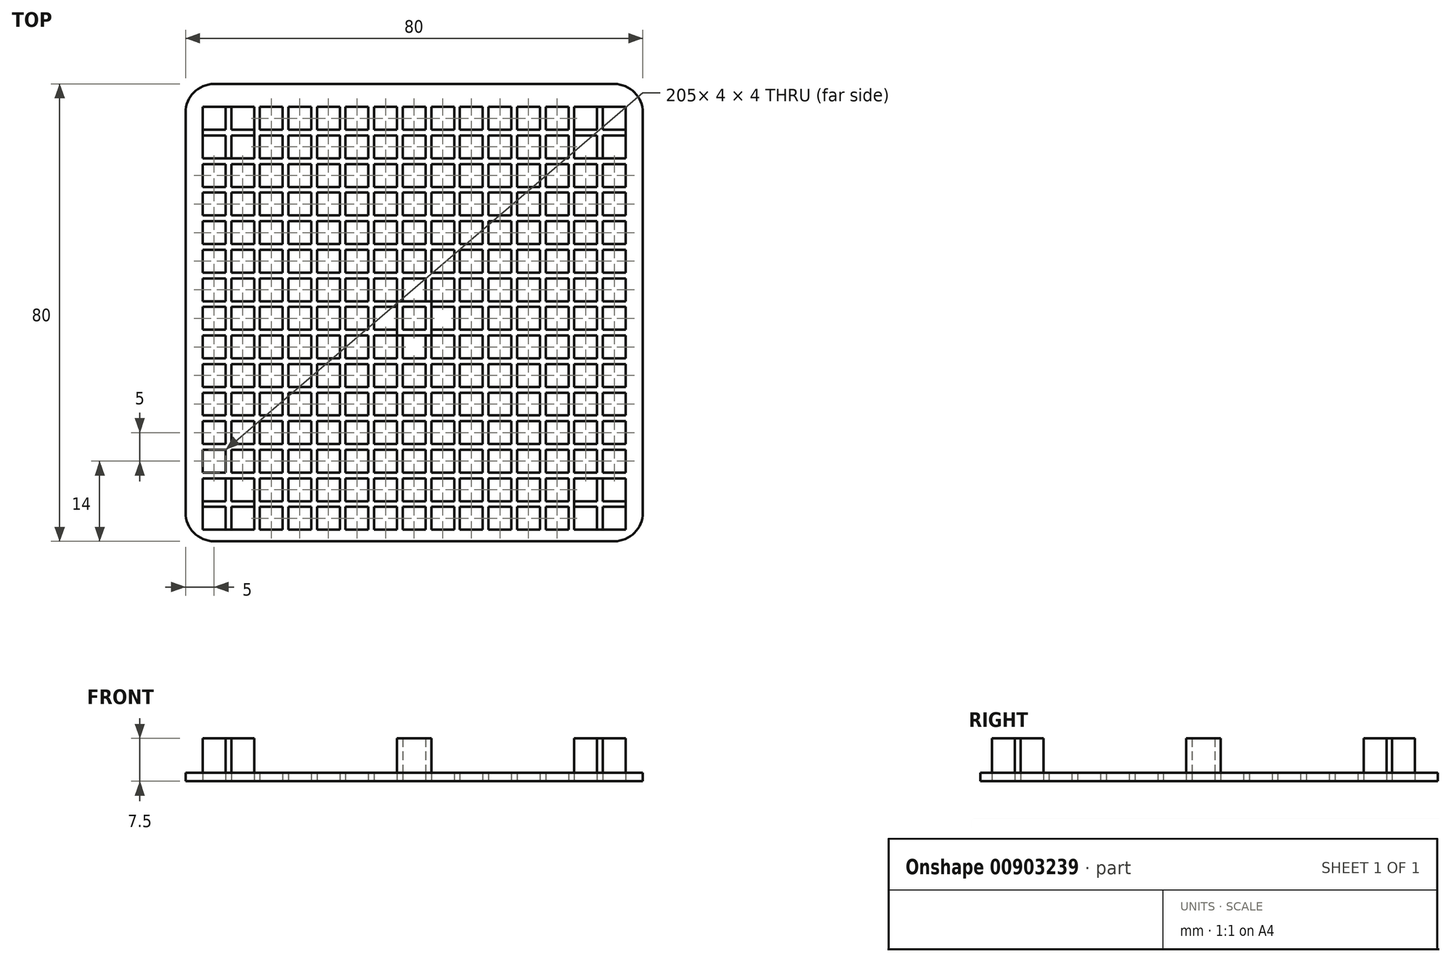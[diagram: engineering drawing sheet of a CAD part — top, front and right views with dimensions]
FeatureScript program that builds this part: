
annotation { "Feature Type Name" : "Feature", "Feature Type Description" : "" }
export const myFeature = defineFeature(function(context is Context, id is Id, definition is map)
    precondition{}
    {
        {
            var Q0;
            Q0=qCreatedBy(makeId("Top.planeOp"),FACE);
            var sketch = newSketch(context, id + "F0", { "sketchPlane" : qUnion([Q0])});
            skLineSegment(sketch, "E0.bottom", {"start": v(40, 40) * mm, "end": v(-40, 40) * mm});
            skLineSegment(sketch, "E0.top", {"start": v(40, -40) * mm, "end": v(-40, -40) * mm});
            skLineSegment(sketch, "E0.left", {"start": v(40, 40) * mm, "end": v(40, -40) * mm});
            skLineSegment(sketch, "E0.right", {"start": v(-40, 40) * mm, "end": v(-40, -40) * mm});
            skPoint(sketch, "E0.middle", {"position": v(0, 0) * mm});
            skLineSegment(sketch, "E1.bottom", {"start": v(-37, 36) * mm, "end": v(-33, 36) * mm});
            skLineSegment(sketch, "E1.top", {"start": v(-37, 32) * mm, "end": v(-33, 32) * mm});
            skLineSegment(sketch, "E1.left", {"start": v(-37, 36) * mm, "end": v(-37, 32) * mm});
            skLineSegment(sketch, "E1.right", {"start": v(-33, 36) * mm, "end": v(-33, 32) * mm});
            skLineSegment(sketch, "E2.0.1.0", {"start": v(-33, 31) * mm, "end": v(-33, 27) * mm});
            skLineSegment(sketch, "E2.0.1.1", {"start": v(-37, 31) * mm, "end": v(-33, 31) * mm});
            skLineSegment(sketch, "E2.0.1.2", {"start": v(-37, 27) * mm, "end": v(-33, 27) * mm});
            skLineSegment(sketch, "E2.0.1.3", {"start": v(-37, 31) * mm, "end": v(-37, 27) * mm});
            skLineSegment(sketch, "E2.0.2.0", {"start": v(-33, 26) * mm, "end": v(-33, 22) * mm});
            skLineSegment(sketch, "E2.0.2.1", {"start": v(-37, 26) * mm, "end": v(-33, 26) * mm});
            skLineSegment(sketch, "E2.0.2.2", {"start": v(-37, 22) * mm, "end": v(-33, 22) * mm});
            skLineSegment(sketch, "E2.0.2.3", {"start": v(-37, 26) * mm, "end": v(-37, 22) * mm});
            skLineSegment(sketch, "E2.0.3.0", {"start": v(-33, 21) * mm, "end": v(-33, 17) * mm});
            skLineSegment(sketch, "E2.0.3.1", {"start": v(-37, 21) * mm, "end": v(-33, 21) * mm});
            skLineSegment(sketch, "E2.0.3.2", {"start": v(-37, 17) * mm, "end": v(-33, 17) * mm});
            skLineSegment(sketch, "E2.0.3.3", {"start": v(-37, 21) * mm, "end": v(-37, 17) * mm});
            skLineSegment(sketch, "E2.0.4.0", {"start": v(-33, 16) * mm, "end": v(-33, 12) * mm});
            skLineSegment(sketch, "E2.0.4.1", {"start": v(-37, 16) * mm, "end": v(-33, 16) * mm});
            skLineSegment(sketch, "E2.0.4.2", {"start": v(-37, 12) * mm, "end": v(-33, 12) * mm});
            skLineSegment(sketch, "E2.0.4.3", {"start": v(-37, 16) * mm, "end": v(-37, 12) * mm});
            skLineSegment(sketch, "E2.0.5.0", {"start": v(-33, 11) * mm, "end": v(-33, 7) * mm});
            skLineSegment(sketch, "E2.0.5.1", {"start": v(-37, 11) * mm, "end": v(-33, 11) * mm});
            skLineSegment(sketch, "E2.0.5.2", {"start": v(-37, 7) * mm, "end": v(-33, 7) * mm});
            skLineSegment(sketch, "E2.0.5.3", {"start": v(-37, 11) * mm, "end": v(-37, 7) * mm});
            skLineSegment(sketch, "E2.0.6.0", {"start": v(-33, 6) * mm, "end": v(-33, 2) * mm});
            skLineSegment(sketch, "E2.0.6.1", {"start": v(-37, 6) * mm, "end": v(-33, 6) * mm});
            skLineSegment(sketch, "E2.0.6.2", {"start": v(-37, 2) * mm, "end": v(-33, 2) * mm});
            skLineSegment(sketch, "E2.0.6.3", {"start": v(-37, 6) * mm, "end": v(-37, 2) * mm});
            skLineSegment(sketch, "E2.0.7.0", {"start": v(-33, 1) * mm, "end": v(-33, -3) * mm});
            skLineSegment(sketch, "E2.0.7.1", {"start": v(-37, 1) * mm, "end": v(-33, 1) * mm});
            skLineSegment(sketch, "E2.0.7.2", {"start": v(-37, -3) * mm, "end": v(-33, -3) * mm});
            skLineSegment(sketch, "E2.0.7.3", {"start": v(-37, 1) * mm, "end": v(-37, -3) * mm});
            skLineSegment(sketch, "E2.1.0.0", {"start": v(-28, 36) * mm, "end": v(-28, 32) * mm});
            skLineSegment(sketch, "E2.1.0.1", {"start": v(-32, 36) * mm, "end": v(-28, 36) * mm});
            skLineSegment(sketch, "E2.1.0.2", {"start": v(-32, 32) * mm, "end": v(-28, 32) * mm});
            skLineSegment(sketch, "E2.1.0.3", {"start": v(-32, 36) * mm, "end": v(-32, 32) * mm});
            skLineSegment(sketch, "E2.1.1.0", {"start": v(-28, 31) * mm, "end": v(-28, 27) * mm});
            skLineSegment(sketch, "E2.1.1.1", {"start": v(-32, 31) * mm, "end": v(-28, 31) * mm});
            skLineSegment(sketch, "E2.1.1.2", {"start": v(-32, 27) * mm, "end": v(-28, 27) * mm});
            skLineSegment(sketch, "E2.1.1.3", {"start": v(-32, 31) * mm, "end": v(-32, 27) * mm});
            skLineSegment(sketch, "E2.1.2.0", {"start": v(-28, 26) * mm, "end": v(-28, 22) * mm});
            skLineSegment(sketch, "E2.1.2.1", {"start": v(-32, 26) * mm, "end": v(-28, 26) * mm});
            skLineSegment(sketch, "E2.1.2.2", {"start": v(-32, 22) * mm, "end": v(-28, 22) * mm});
            skLineSegment(sketch, "E2.1.2.3", {"start": v(-32, 26) * mm, "end": v(-32, 22) * mm});
            skLineSegment(sketch, "E2.1.3.0", {"start": v(-28, 21) * mm, "end": v(-28, 17) * mm});
            skLineSegment(sketch, "E2.1.3.1", {"start": v(-32, 21) * mm, "end": v(-28, 21) * mm});
            skLineSegment(sketch, "E2.1.3.2", {"start": v(-32, 17) * mm, "end": v(-28, 17) * mm});
            skLineSegment(sketch, "E2.1.3.3", {"start": v(-32, 21) * mm, "end": v(-32, 17) * mm});
            skLineSegment(sketch, "E2.1.4.0", {"start": v(-28, 16) * mm, "end": v(-28, 12) * mm});
            skLineSegment(sketch, "E2.1.4.1", {"start": v(-32, 16) * mm, "end": v(-28, 16) * mm});
            skLineSegment(sketch, "E2.1.4.2", {"start": v(-32, 12) * mm, "end": v(-28, 12) * mm});
            skLineSegment(sketch, "E2.1.4.3", {"start": v(-32, 16) * mm, "end": v(-32, 12) * mm});
            skLineSegment(sketch, "E2.1.5.0", {"start": v(-28, 11) * mm, "end": v(-28, 7) * mm});
            skLineSegment(sketch, "E2.1.5.1", {"start": v(-32, 11) * mm, "end": v(-28, 11) * mm});
            skLineSegment(sketch, "E2.1.5.2", {"start": v(-32, 7) * mm, "end": v(-28, 7) * mm});
            skLineSegment(sketch, "E2.1.5.3", {"start": v(-32, 11) * mm, "end": v(-32, 7) * mm});
            skLineSegment(sketch, "E2.1.6.0", {"start": v(-28, 6) * mm, "end": v(-28, 2) * mm});
            skLineSegment(sketch, "E2.1.6.1", {"start": v(-32, 6) * mm, "end": v(-28, 6) * mm});
            skLineSegment(sketch, "E2.1.6.2", {"start": v(-32, 2) * mm, "end": v(-28, 2) * mm});
            skLineSegment(sketch, "E2.1.6.3", {"start": v(-32, 6) * mm, "end": v(-32, 2) * mm});
            skLineSegment(sketch, "E2.1.7.0", {"start": v(-28, 1) * mm, "end": v(-28, -3) * mm});
            skLineSegment(sketch, "E2.1.7.1", {"start": v(-32, 1) * mm, "end": v(-28, 1) * mm});
            skLineSegment(sketch, "E2.1.7.2", {"start": v(-32, -3) * mm, "end": v(-28, -3) * mm});
            skLineSegment(sketch, "E2.1.7.3", {"start": v(-32, 1) * mm, "end": v(-32, -3) * mm});
            skLineSegment(sketch, "E2.2.0.0", {"start": v(-23, 36) * mm, "end": v(-23, 32) * mm});
            skLineSegment(sketch, "E2.2.0.1", {"start": v(-27, 36) * mm, "end": v(-23, 36) * mm});
            skLineSegment(sketch, "E2.2.0.2", {"start": v(-27, 32) * mm, "end": v(-23, 32) * mm});
            skLineSegment(sketch, "E2.2.0.3", {"start": v(-27, 36) * mm, "end": v(-27, 32) * mm});
            skLineSegment(sketch, "E2.2.1.0", {"start": v(-23, 31) * mm, "end": v(-23, 27) * mm});
            skLineSegment(sketch, "E2.2.1.1", {"start": v(-27, 31) * mm, "end": v(-23, 31) * mm});
            skLineSegment(sketch, "E2.2.1.2", {"start": v(-27, 27) * mm, "end": v(-23, 27) * mm});
            skLineSegment(sketch, "E2.2.1.3", {"start": v(-27, 31) * mm, "end": v(-27, 27) * mm});
            skLineSegment(sketch, "E2.2.2.0", {"start": v(-23, 26) * mm, "end": v(-23, 22) * mm});
            skLineSegment(sketch, "E2.2.2.1", {"start": v(-27, 26) * mm, "end": v(-23, 26) * mm});
            skLineSegment(sketch, "E2.2.2.2", {"start": v(-27, 22) * mm, "end": v(-23, 22) * mm});
            skLineSegment(sketch, "E2.2.2.3", {"start": v(-27, 26) * mm, "end": v(-27, 22) * mm});
            skLineSegment(sketch, "E2.2.3.0", {"start": v(-23, 21) * mm, "end": v(-23, 17) * mm});
            skLineSegment(sketch, "E2.2.3.1", {"start": v(-27, 21) * mm, "end": v(-23, 21) * mm});
            skLineSegment(sketch, "E2.2.3.2", {"start": v(-27, 17) * mm, "end": v(-23, 17) * mm});
            skLineSegment(sketch, "E2.2.3.3", {"start": v(-27, 21) * mm, "end": v(-27, 17) * mm});
            skLineSegment(sketch, "E2.2.4.0", {"start": v(-23, 16) * mm, "end": v(-23, 12) * mm});
            skLineSegment(sketch, "E2.2.4.1", {"start": v(-27, 16) * mm, "end": v(-23, 16) * mm});
            skLineSegment(sketch, "E2.2.4.2", {"start": v(-27, 12) * mm, "end": v(-23, 12) * mm});
            skLineSegment(sketch, "E2.2.4.3", {"start": v(-27, 16) * mm, "end": v(-27, 12) * mm});
            skLineSegment(sketch, "E2.2.5.0", {"start": v(-23, 11) * mm, "end": v(-23, 7) * mm});
            skLineSegment(sketch, "E2.2.5.1", {"start": v(-27, 11) * mm, "end": v(-23, 11) * mm});
            skLineSegment(sketch, "E2.2.5.2", {"start": v(-27, 7) * mm, "end": v(-23, 7) * mm});
            skLineSegment(sketch, "E2.2.5.3", {"start": v(-27, 11) * mm, "end": v(-27, 7) * mm});
            skLineSegment(sketch, "E2.2.6.0", {"start": v(-23, 6) * mm, "end": v(-23, 2) * mm});
            skLineSegment(sketch, "E2.2.6.1", {"start": v(-27, 6) * mm, "end": v(-23, 6) * mm});
            skLineSegment(sketch, "E2.2.6.2", {"start": v(-27, 2) * mm, "end": v(-23, 2) * mm});
            skLineSegment(sketch, "E2.2.6.3", {"start": v(-27, 6) * mm, "end": v(-27, 2) * mm});
            skLineSegment(sketch, "E2.2.7.0", {"start": v(-23, 1) * mm, "end": v(-23, -3) * mm});
            skLineSegment(sketch, "E2.2.7.1", {"start": v(-27, 1) * mm, "end": v(-23, 1) * mm});
            skLineSegment(sketch, "E2.2.7.2", {"start": v(-27, -3) * mm, "end": v(-23, -3) * mm});
            skLineSegment(sketch, "E2.2.7.3", {"start": v(-27, 1) * mm, "end": v(-27, -3) * mm});
            skLineSegment(sketch, "E2.3.0.0", {"start": v(-18, 36) * mm, "end": v(-18, 32) * mm});
            skLineSegment(sketch, "E2.3.0.1", {"start": v(-22, 36) * mm, "end": v(-18, 36) * mm});
            skLineSegment(sketch, "E2.3.0.2", {"start": v(-22, 32) * mm, "end": v(-18, 32) * mm});
            skLineSegment(sketch, "E2.3.0.3", {"start": v(-22, 36) * mm, "end": v(-22, 32) * mm});
            skLineSegment(sketch, "E2.3.1.0", {"start": v(-18, 31) * mm, "end": v(-18, 27) * mm});
            skLineSegment(sketch, "E2.3.1.1", {"start": v(-22, 31) * mm, "end": v(-18, 31) * mm});
            skLineSegment(sketch, "E2.3.1.2", {"start": v(-22, 27) * mm, "end": v(-18, 27) * mm});
            skLineSegment(sketch, "E2.3.1.3", {"start": v(-22, 31) * mm, "end": v(-22, 27) * mm});
            skLineSegment(sketch, "E2.3.2.0", {"start": v(-18, 26) * mm, "end": v(-18, 22) * mm});
            skLineSegment(sketch, "E2.3.2.1", {"start": v(-22, 26) * mm, "end": v(-18, 26) * mm});
            skLineSegment(sketch, "E2.3.2.2", {"start": v(-22, 22) * mm, "end": v(-18, 22) * mm});
            skLineSegment(sketch, "E2.3.2.3", {"start": v(-22, 26) * mm, "end": v(-22, 22) * mm});
            skLineSegment(sketch, "E2.3.3.0", {"start": v(-18, 21) * mm, "end": v(-18, 17) * mm});
            skLineSegment(sketch, "E2.3.3.1", {"start": v(-22, 21) * mm, "end": v(-18, 21) * mm});
            skLineSegment(sketch, "E2.3.3.2", {"start": v(-22, 17) * mm, "end": v(-18, 17) * mm});
            skLineSegment(sketch, "E2.3.3.3", {"start": v(-22, 21) * mm, "end": v(-22, 17) * mm});
            skLineSegment(sketch, "E2.3.4.0", {"start": v(-18, 16) * mm, "end": v(-18, 12) * mm});
            skLineSegment(sketch, "E2.3.4.1", {"start": v(-22, 16) * mm, "end": v(-18, 16) * mm});
            skLineSegment(sketch, "E2.3.4.2", {"start": v(-22, 12) * mm, "end": v(-18, 12) * mm});
            skLineSegment(sketch, "E2.3.4.3", {"start": v(-22, 16) * mm, "end": v(-22, 12) * mm});
            skLineSegment(sketch, "E2.3.5.0", {"start": v(-18, 11) * mm, "end": v(-18, 7) * mm});
            skLineSegment(sketch, "E2.3.5.1", {"start": v(-22, 11) * mm, "end": v(-18, 11) * mm});
            skLineSegment(sketch, "E2.3.5.2", {"start": v(-22, 7) * mm, "end": v(-18, 7) * mm});
            skLineSegment(sketch, "E2.3.5.3", {"start": v(-22, 11) * mm, "end": v(-22, 7) * mm});
            skLineSegment(sketch, "E2.3.6.0", {"start": v(-18, 6) * mm, "end": v(-18, 2) * mm});
            skLineSegment(sketch, "E2.3.6.1", {"start": v(-22, 6) * mm, "end": v(-18, 6) * mm});
            skLineSegment(sketch, "E2.3.6.2", {"start": v(-22, 2) * mm, "end": v(-18, 2) * mm});
            skLineSegment(sketch, "E2.3.6.3", {"start": v(-22, 6) * mm, "end": v(-22, 2) * mm});
            skLineSegment(sketch, "E2.3.7.0", {"start": v(-18, 1) * mm, "end": v(-18, -3) * mm});
            skLineSegment(sketch, "E2.3.7.1", {"start": v(-22, 1) * mm, "end": v(-18, 1) * mm});
            skLineSegment(sketch, "E2.3.7.2", {"start": v(-22, -3) * mm, "end": v(-18, -3) * mm});
            skLineSegment(sketch, "E2.3.7.3", {"start": v(-22, 1) * mm, "end": v(-22, -3) * mm});
            skLineSegment(sketch, "E2.4.0.0", {"start": v(-13, 36) * mm, "end": v(-13, 32) * mm});
            skLineSegment(sketch, "E2.4.0.1", {"start": v(-17, 36) * mm, "end": v(-13, 36) * mm});
            skLineSegment(sketch, "E2.4.0.2", {"start": v(-17, 32) * mm, "end": v(-13, 32) * mm});
            skLineSegment(sketch, "E2.4.0.3", {"start": v(-17, 36) * mm, "end": v(-17, 32) * mm});
            skLineSegment(sketch, "E2.4.1.0", {"start": v(-13, 31) * mm, "end": v(-13, 27) * mm});
            skLineSegment(sketch, "E2.4.1.1", {"start": v(-17, 31) * mm, "end": v(-13, 31) * mm});
            skLineSegment(sketch, "E2.4.1.2", {"start": v(-17, 27) * mm, "end": v(-13, 27) * mm});
            skLineSegment(sketch, "E2.4.1.3", {"start": v(-17, 31) * mm, "end": v(-17, 27) * mm});
            skLineSegment(sketch, "E2.4.2.0", {"start": v(-13, 26) * mm, "end": v(-13, 22) * mm});
            skLineSegment(sketch, "E2.4.2.1", {"start": v(-17, 26) * mm, "end": v(-13, 26) * mm});
            skLineSegment(sketch, "E2.4.2.2", {"start": v(-17, 22) * mm, "end": v(-13, 22) * mm});
            skLineSegment(sketch, "E2.4.2.3", {"start": v(-17, 26) * mm, "end": v(-17, 22) * mm});
            skLineSegment(sketch, "E2.4.3.0", {"start": v(-13, 21) * mm, "end": v(-13, 17) * mm});
            skLineSegment(sketch, "E2.4.3.1", {"start": v(-17, 21) * mm, "end": v(-13, 21) * mm});
            skLineSegment(sketch, "E2.4.3.2", {"start": v(-17, 17) * mm, "end": v(-13, 17) * mm});
            skLineSegment(sketch, "E2.4.3.3", {"start": v(-17, 21) * mm, "end": v(-17, 17) * mm});
            skLineSegment(sketch, "E2.4.4.0", {"start": v(-13, 16) * mm, "end": v(-13, 12) * mm});
            skLineSegment(sketch, "E2.4.4.1", {"start": v(-17, 16) * mm, "end": v(-13, 16) * mm});
            skLineSegment(sketch, "E2.4.4.2", {"start": v(-17, 12) * mm, "end": v(-13, 12) * mm});
            skLineSegment(sketch, "E2.4.4.3", {"start": v(-17, 16) * mm, "end": v(-17, 12) * mm});
            skLineSegment(sketch, "E2.4.5.0", {"start": v(-13, 11) * mm, "end": v(-13, 7) * mm});
            skLineSegment(sketch, "E2.4.5.1", {"start": v(-17, 11) * mm, "end": v(-13, 11) * mm});
            skLineSegment(sketch, "E2.4.5.2", {"start": v(-17, 7) * mm, "end": v(-13, 7) * mm});
            skLineSegment(sketch, "E2.4.5.3", {"start": v(-17, 11) * mm, "end": v(-17, 7) * mm});
            skLineSegment(sketch, "E2.4.6.0", {"start": v(-13, 6) * mm, "end": v(-13, 2) * mm});
            skLineSegment(sketch, "E2.4.6.1", {"start": v(-17, 6) * mm, "end": v(-13, 6) * mm});
            skLineSegment(sketch, "E2.4.6.2", {"start": v(-17, 2) * mm, "end": v(-13, 2) * mm});
            skLineSegment(sketch, "E2.4.6.3", {"start": v(-17, 6) * mm, "end": v(-17, 2) * mm});
            skLineSegment(sketch, "E2.4.7.0", {"start": v(-13, 1) * mm, "end": v(-13, -3) * mm});
            skLineSegment(sketch, "E2.4.7.1", {"start": v(-17, 1) * mm, "end": v(-13, 1) * mm});
            skLineSegment(sketch, "E2.4.7.2", {"start": v(-17, -3) * mm, "end": v(-13, -3) * mm});
            skLineSegment(sketch, "E2.4.7.3", {"start": v(-17, 1) * mm, "end": v(-17, -3) * mm});
            skLineSegment(sketch, "E2.5.0.0", {"start": v(-8, 36) * mm, "end": v(-8, 32) * mm});
            skLineSegment(sketch, "E2.5.0.1", {"start": v(-12, 36) * mm, "end": v(-8, 36) * mm});
            skLineSegment(sketch, "E2.5.0.2", {"start": v(-12, 32) * mm, "end": v(-8, 32) * mm});
            skLineSegment(sketch, "E2.5.0.3", {"start": v(-12, 36) * mm, "end": v(-12, 32) * mm});
            skLineSegment(sketch, "E2.5.1.0", {"start": v(-8, 31) * mm, "end": v(-8, 27) * mm});
            skLineSegment(sketch, "E2.5.1.1", {"start": v(-12, 31) * mm, "end": v(-8, 31) * mm});
            skLineSegment(sketch, "E2.5.1.2", {"start": v(-12, 27) * mm, "end": v(-8, 27) * mm});
            skLineSegment(sketch, "E2.5.1.3", {"start": v(-12, 31) * mm, "end": v(-12, 27) * mm});
            skLineSegment(sketch, "E2.5.2.0", {"start": v(-8, 26) * mm, "end": v(-8, 22) * mm});
            skLineSegment(sketch, "E2.5.2.1", {"start": v(-12, 26) * mm, "end": v(-8, 26) * mm});
            skLineSegment(sketch, "E2.5.2.2", {"start": v(-12, 22) * mm, "end": v(-8, 22) * mm});
            skLineSegment(sketch, "E2.5.2.3", {"start": v(-12, 26) * mm, "end": v(-12, 22) * mm});
            skLineSegment(sketch, "E2.5.3.0", {"start": v(-8, 21) * mm, "end": v(-8, 17) * mm});
            skLineSegment(sketch, "E2.5.3.1", {"start": v(-12, 21) * mm, "end": v(-8, 21) * mm});
            skLineSegment(sketch, "E2.5.3.2", {"start": v(-12, 17) * mm, "end": v(-8, 17) * mm});
            skLineSegment(sketch, "E2.5.3.3", {"start": v(-12, 21) * mm, "end": v(-12, 17) * mm});
            skLineSegment(sketch, "E2.5.4.0", {"start": v(-8, 16) * mm, "end": v(-8, 12) * mm});
            skLineSegment(sketch, "E2.5.4.1", {"start": v(-12, 16) * mm, "end": v(-8, 16) * mm});
            skLineSegment(sketch, "E2.5.4.2", {"start": v(-12, 12) * mm, "end": v(-8, 12) * mm});
            skLineSegment(sketch, "E2.5.4.3", {"start": v(-12, 16) * mm, "end": v(-12, 12) * mm});
            skLineSegment(sketch, "E2.5.5.0", {"start": v(-8, 11) * mm, "end": v(-8, 7) * mm});
            skLineSegment(sketch, "E2.5.5.1", {"start": v(-12, 11) * mm, "end": v(-8, 11) * mm});
            skLineSegment(sketch, "E2.5.5.2", {"start": v(-12, 7) * mm, "end": v(-8, 7) * mm});
            skLineSegment(sketch, "E2.5.5.3", {"start": v(-12, 11) * mm, "end": v(-12, 7) * mm});
            skLineSegment(sketch, "E2.5.6.0", {"start": v(-8, 6) * mm, "end": v(-8, 2) * mm});
            skLineSegment(sketch, "E2.5.6.1", {"start": v(-12, 6) * mm, "end": v(-8, 6) * mm});
            skLineSegment(sketch, "E2.5.6.2", {"start": v(-12, 2) * mm, "end": v(-8, 2) * mm});
            skLineSegment(sketch, "E2.5.6.3", {"start": v(-12, 6) * mm, "end": v(-12, 2) * mm});
            skLineSegment(sketch, "E2.5.7.0", {"start": v(-8, 1) * mm, "end": v(-8, -3) * mm});
            skLineSegment(sketch, "E2.5.7.1", {"start": v(-12, 1) * mm, "end": v(-8, 1) * mm});
            skLineSegment(sketch, "E2.5.7.2", {"start": v(-12, -3) * mm, "end": v(-8, -3) * mm});
            skLineSegment(sketch, "E2.5.7.3", {"start": v(-12, 1) * mm, "end": v(-12, -3) * mm});
            skLineSegment(sketch, "E2.6.0.0", {"start": v(-3, 36) * mm, "end": v(-3, 32) * mm});
            skLineSegment(sketch, "E2.6.0.1", {"start": v(-7, 36) * mm, "end": v(-3, 36) * mm});
            skLineSegment(sketch, "E2.6.0.2", {"start": v(-7, 32) * mm, "end": v(-3, 32) * mm});
            skLineSegment(sketch, "E2.6.0.3", {"start": v(-7, 36) * mm, "end": v(-7, 32) * mm});
            skLineSegment(sketch, "E2.6.1.0", {"start": v(-3, 31) * mm, "end": v(-3, 27) * mm});
            skLineSegment(sketch, "E2.6.1.1", {"start": v(-7, 31) * mm, "end": v(-3, 31) * mm});
            skLineSegment(sketch, "E2.6.1.2", {"start": v(-7, 27) * mm, "end": v(-3, 27) * mm});
            skLineSegment(sketch, "E2.6.1.3", {"start": v(-7, 31) * mm, "end": v(-7, 27) * mm});
            skLineSegment(sketch, "E2.6.2.0", {"start": v(-3, 26) * mm, "end": v(-3, 22) * mm});
            skLineSegment(sketch, "E2.6.2.1", {"start": v(-7, 26) * mm, "end": v(-3, 26) * mm});
            skLineSegment(sketch, "E2.6.2.2", {"start": v(-7, 22) * mm, "end": v(-3, 22) * mm});
            skLineSegment(sketch, "E2.6.2.3", {"start": v(-7, 26) * mm, "end": v(-7, 22) * mm});
            skLineSegment(sketch, "E2.6.3.0", {"start": v(-3, 21) * mm, "end": v(-3, 17) * mm});
            skLineSegment(sketch, "E2.6.3.1", {"start": v(-7, 21) * mm, "end": v(-3, 21) * mm});
            skLineSegment(sketch, "E2.6.3.2", {"start": v(-7, 17) * mm, "end": v(-3, 17) * mm});
            skLineSegment(sketch, "E2.6.3.3", {"start": v(-7, 21) * mm, "end": v(-7, 17) * mm});
            skLineSegment(sketch, "E2.6.4.0", {"start": v(-3, 16) * mm, "end": v(-3, 12) * mm});
            skLineSegment(sketch, "E2.6.4.1", {"start": v(-7, 16) * mm, "end": v(-3, 16) * mm});
            skLineSegment(sketch, "E2.6.4.2", {"start": v(-7, 12) * mm, "end": v(-3, 12) * mm});
            skLineSegment(sketch, "E2.6.4.3", {"start": v(-7, 16) * mm, "end": v(-7, 12) * mm});
            skLineSegment(sketch, "E2.6.5.0", {"start": v(-3, 11) * mm, "end": v(-3, 7) * mm});
            skLineSegment(sketch, "E2.6.5.1", {"start": v(-7, 11) * mm, "end": v(-3, 11) * mm});
            skLineSegment(sketch, "E2.6.5.2", {"start": v(-7, 7) * mm, "end": v(-3, 7) * mm});
            skLineSegment(sketch, "E2.6.5.3", {"start": v(-7, 11) * mm, "end": v(-7, 7) * mm});
            skLineSegment(sketch, "E2.6.6.0", {"start": v(-3, 6) * mm, "end": v(-3, 2) * mm});
            skLineSegment(sketch, "E2.6.6.1", {"start": v(-7, 6) * mm, "end": v(-3, 6) * mm});
            skLineSegment(sketch, "E2.6.6.2", {"start": v(-7, 2) * mm, "end": v(-3, 2) * mm});
            skLineSegment(sketch, "E2.6.6.3", {"start": v(-7, 6) * mm, "end": v(-7, 2) * mm});
            skLineSegment(sketch, "E2.6.7.0", {"start": v(-3, 1) * mm, "end": v(-3, -3) * mm});
            skLineSegment(sketch, "E2.6.7.1", {"start": v(-7, 1) * mm, "end": v(-3, 1) * mm});
            skLineSegment(sketch, "E2.6.7.2", {"start": v(-7, -3) * mm, "end": v(-3, -3) * mm});
            skLineSegment(sketch, "E2.6.7.3", {"start": v(-7, 1) * mm, "end": v(-7, -3) * mm});
            skLineSegment(sketch, "E2.7.0.0", {"start": v(2, 36) * mm, "end": v(2, 32) * mm});
            skLineSegment(sketch, "E2.7.0.1", {"start": v(-2, 36) * mm, "end": v(2, 36) * mm});
            skLineSegment(sketch, "E2.7.0.2", {"start": v(-2, 32) * mm, "end": v(2, 32) * mm});
            skLineSegment(sketch, "E2.7.0.3", {"start": v(-2, 36) * mm, "end": v(-2, 32) * mm});
            skLineSegment(sketch, "E2.7.1.0", {"start": v(2, 31) * mm, "end": v(2, 27) * mm});
            skLineSegment(sketch, "E2.7.1.1", {"start": v(-2, 31) * mm, "end": v(2, 31) * mm});
            skLineSegment(sketch, "E2.7.1.2", {"start": v(-2, 27) * mm, "end": v(2, 27) * mm});
            skLineSegment(sketch, "E2.7.1.3", {"start": v(-2, 31) * mm, "end": v(-2, 27) * mm});
            skLineSegment(sketch, "E2.7.2.0", {"start": v(2, 26) * mm, "end": v(2, 22) * mm});
            skLineSegment(sketch, "E2.7.2.1", {"start": v(-2, 26) * mm, "end": v(2, 26) * mm});
            skLineSegment(sketch, "E2.7.2.2", {"start": v(-2, 22) * mm, "end": v(2, 22) * mm});
            skLineSegment(sketch, "E2.7.2.3", {"start": v(-2, 26) * mm, "end": v(-2, 22) * mm});
            skLineSegment(sketch, "E2.7.3.0", {"start": v(2, 21) * mm, "end": v(2, 17) * mm});
            skLineSegment(sketch, "E2.7.3.1", {"start": v(-2, 21) * mm, "end": v(2, 21) * mm});
            skLineSegment(sketch, "E2.7.3.2", {"start": v(-2, 17) * mm, "end": v(2, 17) * mm});
            skLineSegment(sketch, "E2.7.3.3", {"start": v(-2, 21) * mm, "end": v(-2, 17) * mm});
            skLineSegment(sketch, "E2.7.4.0", {"start": v(2, 16) * mm, "end": v(2, 12) * mm});
            skLineSegment(sketch, "E2.7.4.1", {"start": v(-2, 16) * mm, "end": v(2, 16) * mm});
            skLineSegment(sketch, "E2.7.4.2", {"start": v(-2, 12) * mm, "end": v(2, 12) * mm});
            skLineSegment(sketch, "E2.7.4.3", {"start": v(-2, 16) * mm, "end": v(-2, 12) * mm});
            skLineSegment(sketch, "E2.7.5.0", {"start": v(2, 11) * mm, "end": v(2, 7) * mm});
            skLineSegment(sketch, "E2.7.5.1", {"start": v(-2, 11) * mm, "end": v(2, 11) * mm});
            skLineSegment(sketch, "E2.7.5.2", {"start": v(-2, 7) * mm, "end": v(2, 7) * mm});
            skLineSegment(sketch, "E2.7.5.3", {"start": v(-2, 11) * mm, "end": v(-2, 7) * mm});
            skLineSegment(sketch, "E2.7.6.0", {"start": v(2, 6) * mm, "end": v(2, 2) * mm});
            skLineSegment(sketch, "E2.7.6.1", {"start": v(-2, 6) * mm, "end": v(2, 6) * mm});
            skLineSegment(sketch, "E2.7.6.2", {"start": v(-2, 2) * mm, "end": v(2, 2) * mm});
            skLineSegment(sketch, "E2.7.6.3", {"start": v(-2, 6) * mm, "end": v(-2, 2) * mm});
            skLineSegment(sketch, "E2.7.7.0", {"start": v(2, 1) * mm, "end": v(2, -3) * mm});
            skLineSegment(sketch, "E2.7.7.1", {"start": v(-2, 1) * mm, "end": v(2, 1) * mm});
            skLineSegment(sketch, "E2.7.7.2", {"start": v(-2, -3) * mm, "end": v(2, -3) * mm});
            skLineSegment(sketch, "E2.7.7.3", {"start": v(-2, 1) * mm, "end": v(-2, -3) * mm});
            skLineSegment(sketch, "E2.direction1", {"start": v(-37, 32) * mm, "end": v(-32, 32) * mm, "construction": true});
            skLineSegment(sketch, "E2.direction2", {"start": v(-37, 32) * mm, "end": v(-37, 27) * mm, "construction": true});
            skLineSegment(sketch, "E3.0.8.0", {"start": v(7, 36) * mm, "end": v(7, 32) * mm});
            skLineSegment(sketch, "E3.3.8.0", {"start": v(3, 36) * mm, "end": v(7, 36) * mm});
            skLineSegment(sketch, "E3.6.8.0", {"start": v(3, 32) * mm, "end": v(7, 32) * mm});
            skLineSegment(sketch, "E3.9.8.0", {"start": v(3, 36) * mm, "end": v(3, 32) * mm});
            skLineSegment(sketch, "E3.0.8.1", {"start": v(7, 31) * mm, "end": v(7, 27) * mm});
            skLineSegment(sketch, "E3.3.8.1", {"start": v(3, 31) * mm, "end": v(7, 31) * mm});
            skLineSegment(sketch, "E3.6.8.1", {"start": v(3, 27) * mm, "end": v(7, 27) * mm});
            skLineSegment(sketch, "E3.9.8.1", {"start": v(3, 31) * mm, "end": v(3, 27) * mm});
            skLineSegment(sketch, "E3.0.8.2", {"start": v(7, 26) * mm, "end": v(7, 22) * mm});
            skLineSegment(sketch, "E3.3.8.2", {"start": v(3, 26) * mm, "end": v(7, 26) * mm});
            skLineSegment(sketch, "E3.6.8.2", {"start": v(3, 22) * mm, "end": v(7, 22) * mm});
            skLineSegment(sketch, "E3.9.8.2", {"start": v(3, 26) * mm, "end": v(3, 22) * mm});
            skLineSegment(sketch, "E3.0.8.3", {"start": v(7, 21) * mm, "end": v(7, 17) * mm});
            skLineSegment(sketch, "E3.3.8.3", {"start": v(3, 21) * mm, "end": v(7, 21) * mm});
            skLineSegment(sketch, "E3.6.8.3", {"start": v(3, 17) * mm, "end": v(7, 17) * mm});
            skLineSegment(sketch, "E3.9.8.3", {"start": v(3, 21) * mm, "end": v(3, 17) * mm});
            skLineSegment(sketch, "E3.0.8.4", {"start": v(7, 16) * mm, "end": v(7, 12) * mm});
            skLineSegment(sketch, "E3.3.8.4", {"start": v(3, 16) * mm, "end": v(7, 16) * mm});
            skLineSegment(sketch, "E3.6.8.4", {"start": v(3, 12) * mm, "end": v(7, 12) * mm});
            skLineSegment(sketch, "E3.9.8.4", {"start": v(3, 16) * mm, "end": v(3, 12) * mm});
            skLineSegment(sketch, "E3.0.8.5", {"start": v(7, 11) * mm, "end": v(7, 7) * mm});
            skLineSegment(sketch, "E3.3.8.5", {"start": v(3, 11) * mm, "end": v(7, 11) * mm});
            skLineSegment(sketch, "E3.6.8.5", {"start": v(3, 7) * mm, "end": v(7, 7) * mm});
            skLineSegment(sketch, "E3.9.8.5", {"start": v(3, 11) * mm, "end": v(3, 7) * mm});
            skLineSegment(sketch, "E3.0.8.6", {"start": v(7, 6) * mm, "end": v(7, 2) * mm});
            skLineSegment(sketch, "E3.3.8.6", {"start": v(3, 6) * mm, "end": v(7, 6) * mm});
            skLineSegment(sketch, "E3.6.8.6", {"start": v(3, 2) * mm, "end": v(7, 2) * mm});
            skLineSegment(sketch, "E3.9.8.6", {"start": v(3, 6) * mm, "end": v(3, 2) * mm});
            skLineSegment(sketch, "E3.0.8.7", {"start": v(7, 1) * mm, "end": v(7, -3) * mm});
            skLineSegment(sketch, "E3.3.8.7", {"start": v(3, 1) * mm, "end": v(7, 1) * mm});
            skLineSegment(sketch, "E3.6.8.7", {"start": v(3, -3) * mm, "end": v(7, -3) * mm});
            skLineSegment(sketch, "E3.9.8.7", {"start": v(3, 1) * mm, "end": v(3, -3) * mm});
            skLineSegment(sketch, "E4.0.9.0", {"start": v(12, 36) * mm, "end": v(12, 32) * mm});
            skLineSegment(sketch, "E4.3.9.0", {"start": v(8, 36) * mm, "end": v(12, 36) * mm});
            skLineSegment(sketch, "E4.6.9.0", {"start": v(8, 32) * mm, "end": v(12, 32) * mm});
            skLineSegment(sketch, "E4.9.9.0", {"start": v(8, 36) * mm, "end": v(8, 32) * mm});
            skLineSegment(sketch, "E4.0.9.1", {"start": v(12, 31) * mm, "end": v(12, 27) * mm});
            skLineSegment(sketch, "E4.3.9.1", {"start": v(8, 31) * mm, "end": v(12, 31) * mm});
            skLineSegment(sketch, "E4.6.9.1", {"start": v(8, 27) * mm, "end": v(12, 27) * mm});
            skLineSegment(sketch, "E4.9.9.1", {"start": v(8, 31) * mm, "end": v(8, 27) * mm});
            skLineSegment(sketch, "E4.0.9.2", {"start": v(12, 26) * mm, "end": v(12, 22) * mm});
            skLineSegment(sketch, "E4.3.9.2", {"start": v(8, 26) * mm, "end": v(12, 26) * mm});
            skLineSegment(sketch, "E4.6.9.2", {"start": v(8, 22) * mm, "end": v(12, 22) * mm});
            skLineSegment(sketch, "E4.9.9.2", {"start": v(8, 26) * mm, "end": v(8, 22) * mm});
            skLineSegment(sketch, "E4.0.9.3", {"start": v(12, 21) * mm, "end": v(12, 17) * mm});
            skLineSegment(sketch, "E4.3.9.3", {"start": v(8, 21) * mm, "end": v(12, 21) * mm});
            skLineSegment(sketch, "E4.6.9.3", {"start": v(8, 17) * mm, "end": v(12, 17) * mm});
            skLineSegment(sketch, "E4.9.9.3", {"start": v(8, 21) * mm, "end": v(8, 17) * mm});
            skLineSegment(sketch, "E4.0.9.4", {"start": v(12, 16) * mm, "end": v(12, 12) * mm});
            skLineSegment(sketch, "E4.3.9.4", {"start": v(8, 16) * mm, "end": v(12, 16) * mm});
            skLineSegment(sketch, "E4.6.9.4", {"start": v(8, 12) * mm, "end": v(12, 12) * mm});
            skLineSegment(sketch, "E4.9.9.4", {"start": v(8, 16) * mm, "end": v(8, 12) * mm});
            skLineSegment(sketch, "E4.0.9.5", {"start": v(12, 11) * mm, "end": v(12, 7) * mm});
            skLineSegment(sketch, "E4.3.9.5", {"start": v(8, 11) * mm, "end": v(12, 11) * mm});
            skLineSegment(sketch, "E4.6.9.5", {"start": v(8, 7) * mm, "end": v(12, 7) * mm});
            skLineSegment(sketch, "E4.9.9.5", {"start": v(8, 11) * mm, "end": v(8, 7) * mm});
            skLineSegment(sketch, "E4.0.9.6", {"start": v(12, 6) * mm, "end": v(12, 2) * mm});
            skLineSegment(sketch, "E4.3.9.6", {"start": v(8, 6) * mm, "end": v(12, 6) * mm});
            skLineSegment(sketch, "E4.6.9.6", {"start": v(8, 2) * mm, "end": v(12, 2) * mm});
            skLineSegment(sketch, "E4.9.9.6", {"start": v(8, 6) * mm, "end": v(8, 2) * mm});
            skLineSegment(sketch, "E4.0.9.7", {"start": v(12, 1) * mm, "end": v(12, -3) * mm});
            skLineSegment(sketch, "E4.3.9.7", {"start": v(8, 1) * mm, "end": v(12, 1) * mm});
            skLineSegment(sketch, "E4.6.9.7", {"start": v(8, -3) * mm, "end": v(12, -3) * mm});
            skLineSegment(sketch, "E4.9.9.7", {"start": v(8, 1) * mm, "end": v(8, -3) * mm});
            skLineSegment(sketch, "E5.0.10.0", {"start": v(17, 36) * mm, "end": v(17, 32) * mm});
            skLineSegment(sketch, "E5.3.10.0", {"start": v(13, 36) * mm, "end": v(17, 36) * mm});
            skLineSegment(sketch, "E5.6.10.0", {"start": v(13, 32) * mm, "end": v(17, 32) * mm});
            skLineSegment(sketch, "E5.9.10.0", {"start": v(13, 36) * mm, "end": v(13, 32) * mm});
            skLineSegment(sketch, "E5.0.10.1", {"start": v(17, 31) * mm, "end": v(17, 27) * mm});
            skLineSegment(sketch, "E5.3.10.1", {"start": v(13, 31) * mm, "end": v(17, 31) * mm});
            skLineSegment(sketch, "E5.6.10.1", {"start": v(13, 27) * mm, "end": v(17, 27) * mm});
            skLineSegment(sketch, "E5.9.10.1", {"start": v(13, 31) * mm, "end": v(13, 27) * mm});
            skLineSegment(sketch, "E5.0.10.2", {"start": v(17, 26) * mm, "end": v(17, 22) * mm});
            skLineSegment(sketch, "E5.3.10.2", {"start": v(13, 26) * mm, "end": v(17, 26) * mm});
            skLineSegment(sketch, "E5.6.10.2", {"start": v(13, 22) * mm, "end": v(17, 22) * mm});
            skLineSegment(sketch, "E5.9.10.2", {"start": v(13, 26) * mm, "end": v(13, 22) * mm});
            skLineSegment(sketch, "E5.0.10.3", {"start": v(17, 21) * mm, "end": v(17, 17) * mm});
            skLineSegment(sketch, "E5.3.10.3", {"start": v(13, 21) * mm, "end": v(17, 21) * mm});
            skLineSegment(sketch, "E5.6.10.3", {"start": v(13, 17) * mm, "end": v(17, 17) * mm});
            skLineSegment(sketch, "E5.9.10.3", {"start": v(13, 21) * mm, "end": v(13, 17) * mm});
            skLineSegment(sketch, "E5.0.10.4", {"start": v(17, 16) * mm, "end": v(17, 12) * mm});
            skLineSegment(sketch, "E5.3.10.4", {"start": v(13, 16) * mm, "end": v(17, 16) * mm});
            skLineSegment(sketch, "E5.6.10.4", {"start": v(13, 12) * mm, "end": v(17, 12) * mm});
            skLineSegment(sketch, "E5.9.10.4", {"start": v(13, 16) * mm, "end": v(13, 12) * mm});
            skLineSegment(sketch, "E5.0.10.5", {"start": v(17, 11) * mm, "end": v(17, 7) * mm});
            skLineSegment(sketch, "E5.3.10.5", {"start": v(13, 11) * mm, "end": v(17, 11) * mm});
            skLineSegment(sketch, "E5.6.10.5", {"start": v(13, 7) * mm, "end": v(17, 7) * mm});
            skLineSegment(sketch, "E5.9.10.5", {"start": v(13, 11) * mm, "end": v(13, 7) * mm});
            skLineSegment(sketch, "E5.0.10.6", {"start": v(17, 6) * mm, "end": v(17, 2) * mm});
            skLineSegment(sketch, "E5.3.10.6", {"start": v(13, 6) * mm, "end": v(17, 6) * mm});
            skLineSegment(sketch, "E5.6.10.6", {"start": v(13, 2) * mm, "end": v(17, 2) * mm});
            skLineSegment(sketch, "E5.9.10.6", {"start": v(13, 6) * mm, "end": v(13, 2) * mm});
            skLineSegment(sketch, "E5.0.10.7", {"start": v(17, 1) * mm, "end": v(17, -3) * mm});
            skLineSegment(sketch, "E5.3.10.7", {"start": v(13, 1) * mm, "end": v(17, 1) * mm});
            skLineSegment(sketch, "E5.6.10.7", {"start": v(13, -3) * mm, "end": v(17, -3) * mm});
            skLineSegment(sketch, "E5.9.10.7", {"start": v(13, 1) * mm, "end": v(13, -3) * mm});
            skLineSegment(sketch, "E6.0.11.0", {"start": v(22, 36) * mm, "end": v(22, 32) * mm});
            skLineSegment(sketch, "E6.3.11.0", {"start": v(18, 36) * mm, "end": v(22, 36) * mm});
            skLineSegment(sketch, "E6.6.11.0", {"start": v(18, 32) * mm, "end": v(22, 32) * mm});
            skLineSegment(sketch, "E6.9.11.0", {"start": v(18, 36) * mm, "end": v(18, 32) * mm});
            skLineSegment(sketch, "E6.0.11.1", {"start": v(22, 31) * mm, "end": v(22, 27) * mm});
            skLineSegment(sketch, "E6.3.11.1", {"start": v(18, 31) * mm, "end": v(22, 31) * mm});
            skLineSegment(sketch, "E6.6.11.1", {"start": v(18, 27) * mm, "end": v(22, 27) * mm});
            skLineSegment(sketch, "E6.9.11.1", {"start": v(18, 31) * mm, "end": v(18, 27) * mm});
            skLineSegment(sketch, "E6.0.11.2", {"start": v(22, 26) * mm, "end": v(22, 22) * mm});
            skLineSegment(sketch, "E6.3.11.2", {"start": v(18, 26) * mm, "end": v(22, 26) * mm});
            skLineSegment(sketch, "E6.6.11.2", {"start": v(18, 22) * mm, "end": v(22, 22) * mm});
            skLineSegment(sketch, "E6.9.11.2", {"start": v(18, 26) * mm, "end": v(18, 22) * mm});
            skLineSegment(sketch, "E6.0.11.3", {"start": v(22, 21) * mm, "end": v(22, 17) * mm});
            skLineSegment(sketch, "E6.3.11.3", {"start": v(18, 21) * mm, "end": v(22, 21) * mm});
            skLineSegment(sketch, "E6.6.11.3", {"start": v(18, 17) * mm, "end": v(22, 17) * mm});
            skLineSegment(sketch, "E6.9.11.3", {"start": v(18, 21) * mm, "end": v(18, 17) * mm});
            skLineSegment(sketch, "E6.0.11.4", {"start": v(22, 16) * mm, "end": v(22, 12) * mm});
            skLineSegment(sketch, "E6.3.11.4", {"start": v(18, 16) * mm, "end": v(22, 16) * mm});
            skLineSegment(sketch, "E6.6.11.4", {"start": v(18, 12) * mm, "end": v(22, 12) * mm});
            skLineSegment(sketch, "E6.9.11.4", {"start": v(18, 16) * mm, "end": v(18, 12) * mm});
            skLineSegment(sketch, "E6.0.11.5", {"start": v(22, 11) * mm, "end": v(22, 7) * mm});
            skLineSegment(sketch, "E6.3.11.5", {"start": v(18, 11) * mm, "end": v(22, 11) * mm});
            skLineSegment(sketch, "E6.6.11.5", {"start": v(18, 7) * mm, "end": v(22, 7) * mm});
            skLineSegment(sketch, "E6.9.11.5", {"start": v(18, 11) * mm, "end": v(18, 7) * mm});
            skLineSegment(sketch, "E6.0.11.6", {"start": v(22, 6) * mm, "end": v(22, 2) * mm});
            skLineSegment(sketch, "E6.3.11.6", {"start": v(18, 6) * mm, "end": v(22, 6) * mm});
            skLineSegment(sketch, "E6.6.11.6", {"start": v(18, 2) * mm, "end": v(22, 2) * mm});
            skLineSegment(sketch, "E6.9.11.6", {"start": v(18, 6) * mm, "end": v(18, 2) * mm});
            skLineSegment(sketch, "E6.0.11.7", {"start": v(22, 1) * mm, "end": v(22, -3) * mm});
            skLineSegment(sketch, "E6.3.11.7", {"start": v(18, 1) * mm, "end": v(22, 1) * mm});
            skLineSegment(sketch, "E6.6.11.7", {"start": v(18, -3) * mm, "end": v(22, -3) * mm});
            skLineSegment(sketch, "E6.9.11.7", {"start": v(18, 1) * mm, "end": v(18, -3) * mm});
            skLineSegment(sketch, "E7.0.12.0", {"start": v(27, 36) * mm, "end": v(27, 32) * mm});
            skLineSegment(sketch, "E7.3.12.0", {"start": v(23, 36) * mm, "end": v(27, 36) * mm});
            skLineSegment(sketch, "E7.6.12.0", {"start": v(23, 32) * mm, "end": v(27, 32) * mm});
            skLineSegment(sketch, "E7.9.12.0", {"start": v(23, 36) * mm, "end": v(23, 32) * mm});
            skLineSegment(sketch, "E7.0.12.1", {"start": v(27, 31) * mm, "end": v(27, 27) * mm});
            skLineSegment(sketch, "E7.3.12.1", {"start": v(23, 31) * mm, "end": v(27, 31) * mm});
            skLineSegment(sketch, "E7.6.12.1", {"start": v(23, 27) * mm, "end": v(27, 27) * mm});
            skLineSegment(sketch, "E7.9.12.1", {"start": v(23, 31) * mm, "end": v(23, 27) * mm});
            skLineSegment(sketch, "E7.0.12.2", {"start": v(27, 26) * mm, "end": v(27, 22) * mm});
            skLineSegment(sketch, "E7.3.12.2", {"start": v(23, 26) * mm, "end": v(27, 26) * mm});
            skLineSegment(sketch, "E7.6.12.2", {"start": v(23, 22) * mm, "end": v(27, 22) * mm});
            skLineSegment(sketch, "E7.9.12.2", {"start": v(23, 26) * mm, "end": v(23, 22) * mm});
            skLineSegment(sketch, "E7.0.12.3", {"start": v(27, 21) * mm, "end": v(27, 17) * mm});
            skLineSegment(sketch, "E7.3.12.3", {"start": v(23, 21) * mm, "end": v(27, 21) * mm});
            skLineSegment(sketch, "E7.6.12.3", {"start": v(23, 17) * mm, "end": v(27, 17) * mm});
            skLineSegment(sketch, "E7.9.12.3", {"start": v(23, 21) * mm, "end": v(23, 17) * mm});
            skLineSegment(sketch, "E7.0.12.4", {"start": v(27, 16) * mm, "end": v(27, 12) * mm});
            skLineSegment(sketch, "E7.3.12.4", {"start": v(23, 16) * mm, "end": v(27, 16) * mm});
            skLineSegment(sketch, "E7.6.12.4", {"start": v(23, 12) * mm, "end": v(27, 12) * mm});
            skLineSegment(sketch, "E7.9.12.4", {"start": v(23, 16) * mm, "end": v(23, 12) * mm});
            skLineSegment(sketch, "E7.0.12.5", {"start": v(27, 11) * mm, "end": v(27, 7) * mm});
            skLineSegment(sketch, "E7.3.12.5", {"start": v(23, 11) * mm, "end": v(27, 11) * mm});
            skLineSegment(sketch, "E7.6.12.5", {"start": v(23, 7) * mm, "end": v(27, 7) * mm});
            skLineSegment(sketch, "E7.9.12.5", {"start": v(23, 11) * mm, "end": v(23, 7) * mm});
            skLineSegment(sketch, "E7.0.12.6", {"start": v(27, 6) * mm, "end": v(27, 2) * mm});
            skLineSegment(sketch, "E7.3.12.6", {"start": v(23, 6) * mm, "end": v(27, 6) * mm});
            skLineSegment(sketch, "E7.6.12.6", {"start": v(23, 2) * mm, "end": v(27, 2) * mm});
            skLineSegment(sketch, "E7.9.12.6", {"start": v(23, 6) * mm, "end": v(23, 2) * mm});
            skLineSegment(sketch, "E7.0.12.7", {"start": v(27, 1) * mm, "end": v(27, -3) * mm});
            skLineSegment(sketch, "E7.3.12.7", {"start": v(23, 1) * mm, "end": v(27, 1) * mm});
            skLineSegment(sketch, "E7.6.12.7", {"start": v(23, -3) * mm, "end": v(27, -3) * mm});
            skLineSegment(sketch, "E7.9.12.7", {"start": v(23, 1) * mm, "end": v(23, -3) * mm});
            skLineSegment(sketch, "E8.0.13.0", {"start": v(32, 36) * mm, "end": v(32, 32) * mm});
            skLineSegment(sketch, "E8.3.13.0", {"start": v(28, 36) * mm, "end": v(32, 36) * mm});
            skLineSegment(sketch, "E8.6.13.0", {"start": v(28, 32) * mm, "end": v(32, 32) * mm});
            skLineSegment(sketch, "E8.9.13.0", {"start": v(28, 36) * mm, "end": v(28, 32) * mm});
            skLineSegment(sketch, "E8.0.13.1", {"start": v(32, 31) * mm, "end": v(32, 27) * mm});
            skLineSegment(sketch, "E8.3.13.1", {"start": v(28, 31) * mm, "end": v(32, 31) * mm});
            skLineSegment(sketch, "E8.6.13.1", {"start": v(28, 27) * mm, "end": v(32, 27) * mm});
            skLineSegment(sketch, "E8.9.13.1", {"start": v(28, 31) * mm, "end": v(28, 27) * mm});
            skLineSegment(sketch, "E8.0.13.2", {"start": v(32, 26) * mm, "end": v(32, 22) * mm});
            skLineSegment(sketch, "E8.3.13.2", {"start": v(28, 26) * mm, "end": v(32, 26) * mm});
            skLineSegment(sketch, "E8.6.13.2", {"start": v(28, 22) * mm, "end": v(32, 22) * mm});
            skLineSegment(sketch, "E8.9.13.2", {"start": v(28, 26) * mm, "end": v(28, 22) * mm});
            skLineSegment(sketch, "E8.0.13.3", {"start": v(32, 21) * mm, "end": v(32, 17) * mm});
            skLineSegment(sketch, "E8.3.13.3", {"start": v(28, 21) * mm, "end": v(32, 21) * mm});
            skLineSegment(sketch, "E8.6.13.3", {"start": v(28, 17) * mm, "end": v(32, 17) * mm});
            skLineSegment(sketch, "E8.9.13.3", {"start": v(28, 21) * mm, "end": v(28, 17) * mm});
            skLineSegment(sketch, "E8.0.13.4", {"start": v(32, 16) * mm, "end": v(32, 12) * mm});
            skLineSegment(sketch, "E8.3.13.4", {"start": v(28, 16) * mm, "end": v(32, 16) * mm});
            skLineSegment(sketch, "E8.6.13.4", {"start": v(28, 12) * mm, "end": v(32, 12) * mm});
            skLineSegment(sketch, "E8.9.13.4", {"start": v(28, 16) * mm, "end": v(28, 12) * mm});
            skLineSegment(sketch, "E8.0.13.5", {"start": v(32, 11) * mm, "end": v(32, 7) * mm});
            skLineSegment(sketch, "E8.3.13.5", {"start": v(28, 11) * mm, "end": v(32, 11) * mm});
            skLineSegment(sketch, "E8.6.13.5", {"start": v(28, 7) * mm, "end": v(32, 7) * mm});
            skLineSegment(sketch, "E8.9.13.5", {"start": v(28, 11) * mm, "end": v(28, 7) * mm});
            skLineSegment(sketch, "E8.0.13.6", {"start": v(32, 6) * mm, "end": v(32, 2) * mm});
            skLineSegment(sketch, "E8.3.13.6", {"start": v(28, 6) * mm, "end": v(32, 6) * mm});
            skLineSegment(sketch, "E8.6.13.6", {"start": v(28, 2) * mm, "end": v(32, 2) * mm});
            skLineSegment(sketch, "E8.9.13.6", {"start": v(28, 6) * mm, "end": v(28, 2) * mm});
            skLineSegment(sketch, "E8.0.13.7", {"start": v(32, 1) * mm, "end": v(32, -3) * mm});
            skLineSegment(sketch, "E8.3.13.7", {"start": v(28, 1) * mm, "end": v(32, 1) * mm});
            skLineSegment(sketch, "E8.6.13.7", {"start": v(28, -3) * mm, "end": v(32, -3) * mm});
            skLineSegment(sketch, "E8.9.13.7", {"start": v(28, 1) * mm, "end": v(28, -3) * mm});
            skLineSegment(sketch, "E9.0.14.0", {"start": v(37, 36) * mm, "end": v(37, 32) * mm});
            skLineSegment(sketch, "E9.3.14.0", {"start": v(33, 36) * mm, "end": v(37, 36) * mm});
            skLineSegment(sketch, "E9.6.14.0", {"start": v(33, 32) * mm, "end": v(37, 32) * mm});
            skLineSegment(sketch, "E9.9.14.0", {"start": v(33, 36) * mm, "end": v(33, 32) * mm});
            skLineSegment(sketch, "E9.0.14.1", {"start": v(37, 31) * mm, "end": v(37, 27) * mm});
            skLineSegment(sketch, "E9.3.14.1", {"start": v(33, 31) * mm, "end": v(37, 31) * mm});
            skLineSegment(sketch, "E9.6.14.1", {"start": v(33, 27) * mm, "end": v(37, 27) * mm});
            skLineSegment(sketch, "E9.9.14.1", {"start": v(33, 31) * mm, "end": v(33, 27) * mm});
            skLineSegment(sketch, "E9.0.14.2", {"start": v(37, 26) * mm, "end": v(37, 22) * mm});
            skLineSegment(sketch, "E9.3.14.2", {"start": v(33, 26) * mm, "end": v(37, 26) * mm});
            skLineSegment(sketch, "E9.6.14.2", {"start": v(33, 22) * mm, "end": v(37, 22) * mm});
            skLineSegment(sketch, "E9.9.14.2", {"start": v(33, 26) * mm, "end": v(33, 22) * mm});
            skLineSegment(sketch, "E9.0.14.3", {"start": v(37, 21) * mm, "end": v(37, 17) * mm});
            skLineSegment(sketch, "E9.3.14.3", {"start": v(33, 21) * mm, "end": v(37, 21) * mm});
            skLineSegment(sketch, "E9.6.14.3", {"start": v(33, 17) * mm, "end": v(37, 17) * mm});
            skLineSegment(sketch, "E9.9.14.3", {"start": v(33, 21) * mm, "end": v(33, 17) * mm});
            skLineSegment(sketch, "E9.0.14.4", {"start": v(37, 16) * mm, "end": v(37, 12) * mm});
            skLineSegment(sketch, "E9.3.14.4", {"start": v(33, 16) * mm, "end": v(37, 16) * mm});
            skLineSegment(sketch, "E9.6.14.4", {"start": v(33, 12) * mm, "end": v(37, 12) * mm});
            skLineSegment(sketch, "E9.9.14.4", {"start": v(33, 16) * mm, "end": v(33, 12) * mm});
            skLineSegment(sketch, "E9.0.14.5", {"start": v(37, 11) * mm, "end": v(37, 7) * mm});
            skLineSegment(sketch, "E9.3.14.5", {"start": v(33, 11) * mm, "end": v(37, 11) * mm});
            skLineSegment(sketch, "E9.6.14.5", {"start": v(33, 7) * mm, "end": v(37, 7) * mm});
            skLineSegment(sketch, "E9.9.14.5", {"start": v(33, 11) * mm, "end": v(33, 7) * mm});
            skLineSegment(sketch, "E9.0.14.6", {"start": v(37, 6) * mm, "end": v(37, 2) * mm});
            skLineSegment(sketch, "E9.3.14.6", {"start": v(33, 6) * mm, "end": v(37, 6) * mm});
            skLineSegment(sketch, "E9.6.14.6", {"start": v(33, 2) * mm, "end": v(37, 2) * mm});
            skLineSegment(sketch, "E9.9.14.6", {"start": v(33, 6) * mm, "end": v(33, 2) * mm});
            skLineSegment(sketch, "E9.0.14.7", {"start": v(37, 1) * mm, "end": v(37, -3) * mm});
            skLineSegment(sketch, "E9.3.14.7", {"start": v(33, 1) * mm, "end": v(37, 1) * mm});
            skLineSegment(sketch, "E9.6.14.7", {"start": v(33, -3) * mm, "end": v(37, -3) * mm});
            skLineSegment(sketch, "E9.9.14.7", {"start": v(33, 1) * mm, "end": v(33, -3) * mm});
            skLineSegment(sketch, "E10.0.0.8", {"start": v(-33, -4) * mm, "end": v(-33, -8) * mm});
            skLineSegment(sketch, "E10.3.0.8", {"start": v(-37, -4) * mm, "end": v(-33, -4) * mm});
            skLineSegment(sketch, "E10.6.0.8", {"start": v(-37, -8) * mm, "end": v(-33, -8) * mm});
            skLineSegment(sketch, "E10.9.0.8", {"start": v(-37, -4) * mm, "end": v(-37, -8) * mm});
            skLineSegment(sketch, "E10.0.0.9", {"start": v(-33, -9) * mm, "end": v(-33, -13) * mm});
            skLineSegment(sketch, "E10.3.0.9", {"start": v(-37, -9) * mm, "end": v(-33, -9) * mm});
            skLineSegment(sketch, "E10.6.0.9", {"start": v(-37, -13) * mm, "end": v(-33, -13) * mm});
            skLineSegment(sketch, "E10.9.0.9", {"start": v(-37, -9) * mm, "end": v(-37, -13) * mm});
            skLineSegment(sketch, "E10.0.0.10", {"start": v(-33, -14) * mm, "end": v(-33, -18) * mm});
            skLineSegment(sketch, "E10.3.0.10", {"start": v(-37, -14) * mm, "end": v(-33, -14) * mm});
            skLineSegment(sketch, "E10.6.0.10", {"start": v(-37, -18) * mm, "end": v(-33, -18) * mm});
            skLineSegment(sketch, "E10.9.0.10", {"start": v(-37, -14) * mm, "end": v(-37, -18) * mm});
            skLineSegment(sketch, "E10.0.0.11", {"start": v(-33, -19) * mm, "end": v(-33, -23) * mm});
            skLineSegment(sketch, "E10.3.0.11", {"start": v(-37, -19) * mm, "end": v(-33, -19) * mm});
            skLineSegment(sketch, "E10.6.0.11", {"start": v(-37, -23) * mm, "end": v(-33, -23) * mm});
            skLineSegment(sketch, "E10.9.0.11", {"start": v(-37, -19) * mm, "end": v(-37, -23) * mm});
            skLineSegment(sketch, "E10.0.0.12", {"start": v(-33, -24) * mm, "end": v(-33, -28) * mm});
            skLineSegment(sketch, "E10.3.0.12", {"start": v(-37, -24) * mm, "end": v(-33, -24) * mm});
            skLineSegment(sketch, "E10.6.0.12", {"start": v(-37, -28) * mm, "end": v(-33, -28) * mm});
            skLineSegment(sketch, "E10.9.0.12", {"start": v(-37, -24) * mm, "end": v(-37, -28) * mm});
            skLineSegment(sketch, "E10.0.0.13", {"start": v(-33, -29) * mm, "end": v(-33, -33) * mm});
            skLineSegment(sketch, "E10.3.0.13", {"start": v(-37, -29) * mm, "end": v(-33, -29) * mm});
            skLineSegment(sketch, "E10.6.0.13", {"start": v(-37, -33) * mm, "end": v(-33, -33) * mm});
            skLineSegment(sketch, "E10.9.0.13", {"start": v(-37, -29) * mm, "end": v(-37, -33) * mm});
            skLineSegment(sketch, "E10.0.0.14", {"start": v(-33, -34) * mm, "end": v(-33, -38) * mm});
            skLineSegment(sketch, "E10.3.0.14", {"start": v(-37, -34) * mm, "end": v(-33, -34) * mm});
            skLineSegment(sketch, "E10.6.0.14", {"start": v(-37, -38) * mm, "end": v(-33, -38) * mm});
            skLineSegment(sketch, "E10.9.0.14", {"start": v(-37, -34) * mm, "end": v(-37, -38) * mm});
            skLineSegment(sketch, "E10.0.1.8", {"start": v(-28, -4) * mm, "end": v(-28, -8) * mm});
            skLineSegment(sketch, "E10.3.1.8", {"start": v(-32, -4) * mm, "end": v(-28, -4) * mm});
            skLineSegment(sketch, "E10.6.1.8", {"start": v(-32, -8) * mm, "end": v(-28, -8) * mm});
            skLineSegment(sketch, "E10.9.1.8", {"start": v(-32, -4) * mm, "end": v(-32, -8) * mm});
            skLineSegment(sketch, "E10.0.1.9", {"start": v(-28, -9) * mm, "end": v(-28, -13) * mm});
            skLineSegment(sketch, "E10.3.1.9", {"start": v(-32, -9) * mm, "end": v(-28, -9) * mm});
            skLineSegment(sketch, "E10.6.1.9", {"start": v(-32, -13) * mm, "end": v(-28, -13) * mm});
            skLineSegment(sketch, "E10.9.1.9", {"start": v(-32, -9) * mm, "end": v(-32, -13) * mm});
            skLineSegment(sketch, "E10.0.1.10", {"start": v(-28, -14) * mm, "end": v(-28, -18) * mm});
            skLineSegment(sketch, "E10.3.1.10", {"start": v(-32, -14) * mm, "end": v(-28, -14) * mm});
            skLineSegment(sketch, "E10.6.1.10", {"start": v(-32, -18) * mm, "end": v(-28, -18) * mm});
            skLineSegment(sketch, "E10.9.1.10", {"start": v(-32, -14) * mm, "end": v(-32, -18) * mm});
            skLineSegment(sketch, "E10.0.1.11", {"start": v(-28, -19) * mm, "end": v(-28, -23) * mm});
            skLineSegment(sketch, "E10.3.1.11", {"start": v(-32, -19) * mm, "end": v(-28, -19) * mm});
            skLineSegment(sketch, "E10.6.1.11", {"start": v(-32, -23) * mm, "end": v(-28, -23) * mm});
            skLineSegment(sketch, "E10.9.1.11", {"start": v(-32, -19) * mm, "end": v(-32, -23) * mm});
            skLineSegment(sketch, "E10.0.1.12", {"start": v(-28, -24) * mm, "end": v(-28, -28) * mm});
            skLineSegment(sketch, "E10.3.1.12", {"start": v(-32, -24) * mm, "end": v(-28, -24) * mm});
            skLineSegment(sketch, "E10.6.1.12", {"start": v(-32, -28) * mm, "end": v(-28, -28) * mm});
            skLineSegment(sketch, "E10.9.1.12", {"start": v(-32, -24) * mm, "end": v(-32, -28) * mm});
            skLineSegment(sketch, "E10.0.1.13", {"start": v(-28, -29) * mm, "end": v(-28, -33) * mm});
            skLineSegment(sketch, "E10.3.1.13", {"start": v(-32, -29) * mm, "end": v(-28, -29) * mm});
            skLineSegment(sketch, "E10.6.1.13", {"start": v(-32, -33) * mm, "end": v(-28, -33) * mm});
            skLineSegment(sketch, "E10.9.1.13", {"start": v(-32, -29) * mm, "end": v(-32, -33) * mm});
            skLineSegment(sketch, "E10.0.1.14", {"start": v(-28, -34) * mm, "end": v(-28, -38) * mm});
            skLineSegment(sketch, "E10.3.1.14", {"start": v(-32, -34) * mm, "end": v(-28, -34) * mm});
            skLineSegment(sketch, "E10.6.1.14", {"start": v(-32, -38) * mm, "end": v(-28, -38) * mm});
            skLineSegment(sketch, "E10.9.1.14", {"start": v(-32, -34) * mm, "end": v(-32, -38) * mm});
            skLineSegment(sketch, "E10.0.2.8", {"start": v(-23, -4) * mm, "end": v(-23, -8) * mm});
            skLineSegment(sketch, "E10.3.2.8", {"start": v(-27, -4) * mm, "end": v(-23, -4) * mm});
            skLineSegment(sketch, "E10.6.2.8", {"start": v(-27, -8) * mm, "end": v(-23, -8) * mm});
            skLineSegment(sketch, "E10.9.2.8", {"start": v(-27, -4) * mm, "end": v(-27, -8) * mm});
            skLineSegment(sketch, "E10.0.2.9", {"start": v(-23, -9) * mm, "end": v(-23, -13) * mm});
            skLineSegment(sketch, "E10.3.2.9", {"start": v(-27, -9) * mm, "end": v(-23, -9) * mm});
            skLineSegment(sketch, "E10.6.2.9", {"start": v(-27, -13) * mm, "end": v(-23, -13) * mm});
            skLineSegment(sketch, "E10.9.2.9", {"start": v(-27, -9) * mm, "end": v(-27, -13) * mm});
            skLineSegment(sketch, "E10.0.2.10", {"start": v(-23, -14) * mm, "end": v(-23, -18) * mm});
            skLineSegment(sketch, "E10.3.2.10", {"start": v(-27, -14) * mm, "end": v(-23, -14) * mm});
            skLineSegment(sketch, "E10.6.2.10", {"start": v(-27, -18) * mm, "end": v(-23, -18) * mm});
            skLineSegment(sketch, "E10.9.2.10", {"start": v(-27, -14) * mm, "end": v(-27, -18) * mm});
            skLineSegment(sketch, "E10.0.2.11", {"start": v(-23, -19) * mm, "end": v(-23, -23) * mm});
            skLineSegment(sketch, "E10.3.2.11", {"start": v(-27, -19) * mm, "end": v(-23, -19) * mm});
            skLineSegment(sketch, "E10.6.2.11", {"start": v(-27, -23) * mm, "end": v(-23, -23) * mm});
            skLineSegment(sketch, "E10.9.2.11", {"start": v(-27, -19) * mm, "end": v(-27, -23) * mm});
            skLineSegment(sketch, "E10.0.2.12", {"start": v(-23, -24) * mm, "end": v(-23, -28) * mm});
            skLineSegment(sketch, "E10.3.2.12", {"start": v(-27, -24) * mm, "end": v(-23, -24) * mm});
            skLineSegment(sketch, "E10.6.2.12", {"start": v(-27, -28) * mm, "end": v(-23, -28) * mm});
            skLineSegment(sketch, "E10.9.2.12", {"start": v(-27, -24) * mm, "end": v(-27, -28) * mm});
            skLineSegment(sketch, "E10.0.2.13", {"start": v(-23, -29) * mm, "end": v(-23, -33) * mm});
            skLineSegment(sketch, "E10.3.2.13", {"start": v(-27, -29) * mm, "end": v(-23, -29) * mm});
            skLineSegment(sketch, "E10.6.2.13", {"start": v(-27, -33) * mm, "end": v(-23, -33) * mm});
            skLineSegment(sketch, "E10.9.2.13", {"start": v(-27, -29) * mm, "end": v(-27, -33) * mm});
            skLineSegment(sketch, "E10.0.2.14", {"start": v(-23, -34) * mm, "end": v(-23, -38) * mm});
            skLineSegment(sketch, "E10.3.2.14", {"start": v(-27, -34) * mm, "end": v(-23, -34) * mm});
            skLineSegment(sketch, "E10.6.2.14", {"start": v(-27, -38) * mm, "end": v(-23, -38) * mm});
            skLineSegment(sketch, "E10.9.2.14", {"start": v(-27, -34) * mm, "end": v(-27, -38) * mm});
            skLineSegment(sketch, "E10.0.3.8", {"start": v(-18, -4) * mm, "end": v(-18, -8) * mm});
            skLineSegment(sketch, "E10.3.3.8", {"start": v(-22, -4) * mm, "end": v(-18, -4) * mm});
            skLineSegment(sketch, "E10.6.3.8", {"start": v(-22, -8) * mm, "end": v(-18, -8) * mm});
            skLineSegment(sketch, "E10.9.3.8", {"start": v(-22, -4) * mm, "end": v(-22, -8) * mm});
            skLineSegment(sketch, "E10.0.3.9", {"start": v(-18, -9) * mm, "end": v(-18, -13) * mm});
            skLineSegment(sketch, "E10.3.3.9", {"start": v(-22, -9) * mm, "end": v(-18, -9) * mm});
            skLineSegment(sketch, "E10.6.3.9", {"start": v(-22, -13) * mm, "end": v(-18, -13) * mm});
            skLineSegment(sketch, "E10.9.3.9", {"start": v(-22, -9) * mm, "end": v(-22, -13) * mm});
            skLineSegment(sketch, "E10.0.3.10", {"start": v(-18, -14) * mm, "end": v(-18, -18) * mm});
            skLineSegment(sketch, "E10.3.3.10", {"start": v(-22, -14) * mm, "end": v(-18, -14) * mm});
            skLineSegment(sketch, "E10.6.3.10", {"start": v(-22, -18) * mm, "end": v(-18, -18) * mm});
            skLineSegment(sketch, "E10.9.3.10", {"start": v(-22, -14) * mm, "end": v(-22, -18) * mm});
            skLineSegment(sketch, "E10.0.3.11", {"start": v(-18, -19) * mm, "end": v(-18, -23) * mm});
            skLineSegment(sketch, "E10.3.3.11", {"start": v(-22, -19) * mm, "end": v(-18, -19) * mm});
            skLineSegment(sketch, "E10.6.3.11", {"start": v(-22, -23) * mm, "end": v(-18, -23) * mm});
            skLineSegment(sketch, "E10.9.3.11", {"start": v(-22, -19) * mm, "end": v(-22, -23) * mm});
            skLineSegment(sketch, "E10.0.3.12", {"start": v(-18, -24) * mm, "end": v(-18, -28) * mm});
            skLineSegment(sketch, "E10.3.3.12", {"start": v(-22, -24) * mm, "end": v(-18, -24) * mm});
            skLineSegment(sketch, "E10.6.3.12", {"start": v(-22, -28) * mm, "end": v(-18, -28) * mm});
            skLineSegment(sketch, "E10.9.3.12", {"start": v(-22, -24) * mm, "end": v(-22, -28) * mm});
            skLineSegment(sketch, "E10.0.3.13", {"start": v(-18, -29) * mm, "end": v(-18, -33) * mm});
            skLineSegment(sketch, "E10.3.3.13", {"start": v(-22, -29) * mm, "end": v(-18, -29) * mm});
            skLineSegment(sketch, "E10.6.3.13", {"start": v(-22, -33) * mm, "end": v(-18, -33) * mm});
            skLineSegment(sketch, "E10.9.3.13", {"start": v(-22, -29) * mm, "end": v(-22, -33) * mm});
            skLineSegment(sketch, "E10.0.3.14", {"start": v(-18, -34) * mm, "end": v(-18, -38) * mm});
            skLineSegment(sketch, "E10.3.3.14", {"start": v(-22, -34) * mm, "end": v(-18, -34) * mm});
            skLineSegment(sketch, "E10.6.3.14", {"start": v(-22, -38) * mm, "end": v(-18, -38) * mm});
            skLineSegment(sketch, "E10.9.3.14", {"start": v(-22, -34) * mm, "end": v(-22, -38) * mm});
            skLineSegment(sketch, "E10.0.4.8", {"start": v(-13, -4) * mm, "end": v(-13, -8) * mm});
            skLineSegment(sketch, "E10.3.4.8", {"start": v(-17, -4) * mm, "end": v(-13, -4) * mm});
            skLineSegment(sketch, "E10.6.4.8", {"start": v(-17, -8) * mm, "end": v(-13, -8) * mm});
            skLineSegment(sketch, "E10.9.4.8", {"start": v(-17, -4) * mm, "end": v(-17, -8) * mm});
            skLineSegment(sketch, "E10.0.4.9", {"start": v(-13, -9) * mm, "end": v(-13, -13) * mm});
            skLineSegment(sketch, "E10.3.4.9", {"start": v(-17, -9) * mm, "end": v(-13, -9) * mm});
            skLineSegment(sketch, "E10.6.4.9", {"start": v(-17, -13) * mm, "end": v(-13, -13) * mm});
            skLineSegment(sketch, "E10.9.4.9", {"start": v(-17, -9) * mm, "end": v(-17, -13) * mm});
            skLineSegment(sketch, "E10.0.4.10", {"start": v(-13, -14) * mm, "end": v(-13, -18) * mm});
            skLineSegment(sketch, "E10.3.4.10", {"start": v(-17, -14) * mm, "end": v(-13, -14) * mm});
            skLineSegment(sketch, "E10.6.4.10", {"start": v(-17, -18) * mm, "end": v(-13, -18) * mm});
            skLineSegment(sketch, "E10.9.4.10", {"start": v(-17, -14) * mm, "end": v(-17, -18) * mm});
            skLineSegment(sketch, "E10.0.4.11", {"start": v(-13, -19) * mm, "end": v(-13, -23) * mm});
            skLineSegment(sketch, "E10.3.4.11", {"start": v(-17, -19) * mm, "end": v(-13, -19) * mm});
            skLineSegment(sketch, "E10.6.4.11", {"start": v(-17, -23) * mm, "end": v(-13, -23) * mm});
            skLineSegment(sketch, "E10.9.4.11", {"start": v(-17, -19) * mm, "end": v(-17, -23) * mm});
            skLineSegment(sketch, "E10.0.4.12", {"start": v(-13, -24) * mm, "end": v(-13, -28) * mm});
            skLineSegment(sketch, "E10.3.4.12", {"start": v(-17, -24) * mm, "end": v(-13, -24) * mm});
            skLineSegment(sketch, "E10.6.4.12", {"start": v(-17, -28) * mm, "end": v(-13, -28) * mm});
            skLineSegment(sketch, "E10.9.4.12", {"start": v(-17, -24) * mm, "end": v(-17, -28) * mm});
            skLineSegment(sketch, "E10.0.4.13", {"start": v(-13, -29) * mm, "end": v(-13, -33) * mm});
            skLineSegment(sketch, "E10.3.4.13", {"start": v(-17, -29) * mm, "end": v(-13, -29) * mm});
            skLineSegment(sketch, "E10.6.4.13", {"start": v(-17, -33) * mm, "end": v(-13, -33) * mm});
            skLineSegment(sketch, "E10.9.4.13", {"start": v(-17, -29) * mm, "end": v(-17, -33) * mm});
            skLineSegment(sketch, "E10.0.4.14", {"start": v(-13, -34) * mm, "end": v(-13, -38) * mm});
            skLineSegment(sketch, "E10.3.4.14", {"start": v(-17, -34) * mm, "end": v(-13, -34) * mm});
            skLineSegment(sketch, "E10.6.4.14", {"start": v(-17, -38) * mm, "end": v(-13, -38) * mm});
            skLineSegment(sketch, "E10.9.4.14", {"start": v(-17, -34) * mm, "end": v(-17, -38) * mm});
            skLineSegment(sketch, "E10.0.5.8", {"start": v(-8, -4) * mm, "end": v(-8, -8) * mm});
            skLineSegment(sketch, "E10.3.5.8", {"start": v(-12, -4) * mm, "end": v(-8, -4) * mm});
            skLineSegment(sketch, "E10.6.5.8", {"start": v(-12, -8) * mm, "end": v(-8, -8) * mm});
            skLineSegment(sketch, "E10.9.5.8", {"start": v(-12, -4) * mm, "end": v(-12, -8) * mm});
            skLineSegment(sketch, "E10.0.5.9", {"start": v(-8, -9) * mm, "end": v(-8, -13) * mm});
            skLineSegment(sketch, "E10.3.5.9", {"start": v(-12, -9) * mm, "end": v(-8, -9) * mm});
            skLineSegment(sketch, "E10.6.5.9", {"start": v(-12, -13) * mm, "end": v(-8, -13) * mm});
            skLineSegment(sketch, "E10.9.5.9", {"start": v(-12, -9) * mm, "end": v(-12, -13) * mm});
            skLineSegment(sketch, "E10.0.5.10", {"start": v(-8, -14) * mm, "end": v(-8, -18) * mm});
            skLineSegment(sketch, "E10.3.5.10", {"start": v(-12, -14) * mm, "end": v(-8, -14) * mm});
            skLineSegment(sketch, "E10.6.5.10", {"start": v(-12, -18) * mm, "end": v(-8, -18) * mm});
            skLineSegment(sketch, "E10.9.5.10", {"start": v(-12, -14) * mm, "end": v(-12, -18) * mm});
            skLineSegment(sketch, "E10.0.5.11", {"start": v(-8, -19) * mm, "end": v(-8, -23) * mm});
            skLineSegment(sketch, "E10.3.5.11", {"start": v(-12, -19) * mm, "end": v(-8, -19) * mm});
            skLineSegment(sketch, "E10.6.5.11", {"start": v(-12, -23) * mm, "end": v(-8, -23) * mm});
            skLineSegment(sketch, "E10.9.5.11", {"start": v(-12, -19) * mm, "end": v(-12, -23) * mm});
            skLineSegment(sketch, "E10.0.5.12", {"start": v(-8, -24) * mm, "end": v(-8, -28) * mm});
            skLineSegment(sketch, "E10.3.5.12", {"start": v(-12, -24) * mm, "end": v(-8, -24) * mm});
            skLineSegment(sketch, "E10.6.5.12", {"start": v(-12, -28) * mm, "end": v(-8, -28) * mm});
            skLineSegment(sketch, "E10.9.5.12", {"start": v(-12, -24) * mm, "end": v(-12, -28) * mm});
            skLineSegment(sketch, "E10.0.5.13", {"start": v(-8, -29) * mm, "end": v(-8, -33) * mm});
            skLineSegment(sketch, "E10.3.5.13", {"start": v(-12, -29) * mm, "end": v(-8, -29) * mm});
            skLineSegment(sketch, "E10.6.5.13", {"start": v(-12, -33) * mm, "end": v(-8, -33) * mm});
            skLineSegment(sketch, "E10.9.5.13", {"start": v(-12, -29) * mm, "end": v(-12, -33) * mm});
            skLineSegment(sketch, "E10.0.5.14", {"start": v(-8, -34) * mm, "end": v(-8, -38) * mm});
            skLineSegment(sketch, "E10.3.5.14", {"start": v(-12, -34) * mm, "end": v(-8, -34) * mm});
            skLineSegment(sketch, "E10.6.5.14", {"start": v(-12, -38) * mm, "end": v(-8, -38) * mm});
            skLineSegment(sketch, "E10.9.5.14", {"start": v(-12, -34) * mm, "end": v(-12, -38) * mm});
            skLineSegment(sketch, "E10.0.6.8", {"start": v(-3, -4) * mm, "end": v(-3, -8) * mm});
            skLineSegment(sketch, "E10.3.6.8", {"start": v(-7, -4) * mm, "end": v(-3, -4) * mm});
            skLineSegment(sketch, "E10.6.6.8", {"start": v(-7, -8) * mm, "end": v(-3, -8) * mm});
            skLineSegment(sketch, "E10.9.6.8", {"start": v(-7, -4) * mm, "end": v(-7, -8) * mm});
            skLineSegment(sketch, "E10.0.6.9", {"start": v(-3, -9) * mm, "end": v(-3, -13) * mm});
            skLineSegment(sketch, "E10.3.6.9", {"start": v(-7, -9) * mm, "end": v(-3, -9) * mm});
            skLineSegment(sketch, "E10.6.6.9", {"start": v(-7, -13) * mm, "end": v(-3, -13) * mm});
            skLineSegment(sketch, "E10.9.6.9", {"start": v(-7, -9) * mm, "end": v(-7, -13) * mm});
            skLineSegment(sketch, "E10.0.6.10", {"start": v(-3, -14) * mm, "end": v(-3, -18) * mm});
            skLineSegment(sketch, "E10.3.6.10", {"start": v(-7, -14) * mm, "end": v(-3, -14) * mm});
            skLineSegment(sketch, "E10.6.6.10", {"start": v(-7, -18) * mm, "end": v(-3, -18) * mm});
            skLineSegment(sketch, "E10.9.6.10", {"start": v(-7, -14) * mm, "end": v(-7, -18) * mm});
            skLineSegment(sketch, "E10.0.6.11", {"start": v(-3, -19) * mm, "end": v(-3, -23) * mm});
            skLineSegment(sketch, "E10.3.6.11", {"start": v(-7, -19) * mm, "end": v(-3, -19) * mm});
            skLineSegment(sketch, "E10.6.6.11", {"start": v(-7, -23) * mm, "end": v(-3, -23) * mm});
            skLineSegment(sketch, "E10.9.6.11", {"start": v(-7, -19) * mm, "end": v(-7, -23) * mm});
            skLineSegment(sketch, "E10.0.6.12", {"start": v(-3, -24) * mm, "end": v(-3, -28) * mm});
            skLineSegment(sketch, "E10.3.6.12", {"start": v(-7, -24) * mm, "end": v(-3, -24) * mm});
            skLineSegment(sketch, "E10.6.6.12", {"start": v(-7, -28) * mm, "end": v(-3, -28) * mm});
            skLineSegment(sketch, "E10.9.6.12", {"start": v(-7, -24) * mm, "end": v(-7, -28) * mm});
            skLineSegment(sketch, "E10.0.6.13", {"start": v(-3, -29) * mm, "end": v(-3, -33) * mm});
            skLineSegment(sketch, "E10.3.6.13", {"start": v(-7, -29) * mm, "end": v(-3, -29) * mm});
            skLineSegment(sketch, "E10.6.6.13", {"start": v(-7, -33) * mm, "end": v(-3, -33) * mm});
            skLineSegment(sketch, "E10.9.6.13", {"start": v(-7, -29) * mm, "end": v(-7, -33) * mm});
            skLineSegment(sketch, "E10.0.6.14", {"start": v(-3, -34) * mm, "end": v(-3, -38) * mm});
            skLineSegment(sketch, "E10.3.6.14", {"start": v(-7, -34) * mm, "end": v(-3, -34) * mm});
            skLineSegment(sketch, "E10.6.6.14", {"start": v(-7, -38) * mm, "end": v(-3, -38) * mm});
            skLineSegment(sketch, "E10.9.6.14", {"start": v(-7, -34) * mm, "end": v(-7, -38) * mm});
            skLineSegment(sketch, "E10.0.7.8", {"start": v(2, -4) * mm, "end": v(2, -8) * mm});
            skLineSegment(sketch, "E10.3.7.8", {"start": v(-2, -4) * mm, "end": v(2, -4) * mm});
            skLineSegment(sketch, "E10.6.7.8", {"start": v(-2, -8) * mm, "end": v(2, -8) * mm});
            skLineSegment(sketch, "E10.9.7.8", {"start": v(-2, -4) * mm, "end": v(-2, -8) * mm});
            skLineSegment(sketch, "E10.0.7.9", {"start": v(2, -9) * mm, "end": v(2, -13) * mm});
            skLineSegment(sketch, "E10.3.7.9", {"start": v(-2, -9) * mm, "end": v(2, -9) * mm});
            skLineSegment(sketch, "E10.6.7.9", {"start": v(-2, -13) * mm, "end": v(2, -13) * mm});
            skLineSegment(sketch, "E10.9.7.9", {"start": v(-2, -9) * mm, "end": v(-2, -13) * mm});
            skLineSegment(sketch, "E10.0.7.10", {"start": v(2, -14) * mm, "end": v(2, -18) * mm});
            skLineSegment(sketch, "E10.3.7.10", {"start": v(-2, -14) * mm, "end": v(2, -14) * mm});
            skLineSegment(sketch, "E10.6.7.10", {"start": v(-2, -18) * mm, "end": v(2, -18) * mm});
            skLineSegment(sketch, "E10.9.7.10", {"start": v(-2, -14) * mm, "end": v(-2, -18) * mm});
            skLineSegment(sketch, "E10.0.7.11", {"start": v(2, -19) * mm, "end": v(2, -23) * mm});
            skLineSegment(sketch, "E10.3.7.11", {"start": v(-2, -19) * mm, "end": v(2, -19) * mm});
            skLineSegment(sketch, "E10.6.7.11", {"start": v(-2, -23) * mm, "end": v(2, -23) * mm});
            skLineSegment(sketch, "E10.9.7.11", {"start": v(-2, -19) * mm, "end": v(-2, -23) * mm});
            skLineSegment(sketch, "E10.0.7.12", {"start": v(2, -24) * mm, "end": v(2, -28) * mm});
            skLineSegment(sketch, "E10.3.7.12", {"start": v(-2, -24) * mm, "end": v(2, -24) * mm});
            skLineSegment(sketch, "E10.6.7.12", {"start": v(-2, -28) * mm, "end": v(2, -28) * mm});
            skLineSegment(sketch, "E10.9.7.12", {"start": v(-2, -24) * mm, "end": v(-2, -28) * mm});
            skLineSegment(sketch, "E10.0.7.13", {"start": v(2, -29) * mm, "end": v(2, -33) * mm});
            skLineSegment(sketch, "E10.3.7.13", {"start": v(-2, -29) * mm, "end": v(2, -29) * mm});
            skLineSegment(sketch, "E10.6.7.13", {"start": v(-2, -33) * mm, "end": v(2, -33) * mm});
            skLineSegment(sketch, "E10.9.7.13", {"start": v(-2, -29) * mm, "end": v(-2, -33) * mm});
            skLineSegment(sketch, "E10.0.7.14", {"start": v(2, -34) * mm, "end": v(2, -38) * mm});
            skLineSegment(sketch, "E10.3.7.14", {"start": v(-2, -34) * mm, "end": v(2, -34) * mm});
            skLineSegment(sketch, "E10.6.7.14", {"start": v(-2, -38) * mm, "end": v(2, -38) * mm});
            skLineSegment(sketch, "E10.9.7.14", {"start": v(-2, -34) * mm, "end": v(-2, -38) * mm});
            skLineSegment(sketch, "E10.0.8.8", {"start": v(7, -4) * mm, "end": v(7, -8) * mm});
            skLineSegment(sketch, "E10.3.8.8", {"start": v(3, -4) * mm, "end": v(7, -4) * mm});
            skLineSegment(sketch, "E10.6.8.8", {"start": v(3, -8) * mm, "end": v(7, -8) * mm});
            skLineSegment(sketch, "E10.9.8.8", {"start": v(3, -4) * mm, "end": v(3, -8) * mm});
            skLineSegment(sketch, "E10.0.8.9", {"start": v(7, -9) * mm, "end": v(7, -13) * mm});
            skLineSegment(sketch, "E10.3.8.9", {"start": v(3, -9) * mm, "end": v(7, -9) * mm});
            skLineSegment(sketch, "E10.6.8.9", {"start": v(3, -13) * mm, "end": v(7, -13) * mm});
            skLineSegment(sketch, "E10.9.8.9", {"start": v(3, -9) * mm, "end": v(3, -13) * mm});
            skLineSegment(sketch, "E10.0.8.10", {"start": v(7, -14) * mm, "end": v(7, -18) * mm});
            skLineSegment(sketch, "E10.3.8.10", {"start": v(3, -14) * mm, "end": v(7, -14) * mm});
            skLineSegment(sketch, "E10.6.8.10", {"start": v(3, -18) * mm, "end": v(7, -18) * mm});
            skLineSegment(sketch, "E10.9.8.10", {"start": v(3, -14) * mm, "end": v(3, -18) * mm});
            skLineSegment(sketch, "E10.0.8.11", {"start": v(7, -19) * mm, "end": v(7, -23) * mm});
            skLineSegment(sketch, "E10.3.8.11", {"start": v(3, -19) * mm, "end": v(7, -19) * mm});
            skLineSegment(sketch, "E10.6.8.11", {"start": v(3, -23) * mm, "end": v(7, -23) * mm});
            skLineSegment(sketch, "E10.9.8.11", {"start": v(3, -19) * mm, "end": v(3, -23) * mm});
            skLineSegment(sketch, "E10.0.8.12", {"start": v(7, -24) * mm, "end": v(7, -28) * mm});
            skLineSegment(sketch, "E10.3.8.12", {"start": v(3, -24) * mm, "end": v(7, -24) * mm});
            skLineSegment(sketch, "E10.6.8.12", {"start": v(3, -28) * mm, "end": v(7, -28) * mm});
            skLineSegment(sketch, "E10.9.8.12", {"start": v(3, -24) * mm, "end": v(3, -28) * mm});
            skLineSegment(sketch, "E10.0.8.13", {"start": v(7, -29) * mm, "end": v(7, -33) * mm});
            skLineSegment(sketch, "E10.3.8.13", {"start": v(3, -29) * mm, "end": v(7, -29) * mm});
            skLineSegment(sketch, "E10.6.8.13", {"start": v(3, -33) * mm, "end": v(7, -33) * mm});
            skLineSegment(sketch, "E10.9.8.13", {"start": v(3, -29) * mm, "end": v(3, -33) * mm});
            skLineSegment(sketch, "E10.0.8.14", {"start": v(7, -34) * mm, "end": v(7, -38) * mm});
            skLineSegment(sketch, "E10.3.8.14", {"start": v(3, -34) * mm, "end": v(7, -34) * mm});
            skLineSegment(sketch, "E10.6.8.14", {"start": v(3, -38) * mm, "end": v(7, -38) * mm});
            skLineSegment(sketch, "E10.9.8.14", {"start": v(3, -34) * mm, "end": v(3, -38) * mm});
            skLineSegment(sketch, "E10.0.9.8", {"start": v(12, -4) * mm, "end": v(12, -8) * mm});
            skLineSegment(sketch, "E10.3.9.8", {"start": v(8, -4) * mm, "end": v(12, -4) * mm});
            skLineSegment(sketch, "E10.6.9.8", {"start": v(8, -8) * mm, "end": v(12, -8) * mm});
            skLineSegment(sketch, "E10.9.9.8", {"start": v(8, -4) * mm, "end": v(8, -8) * mm});
            skLineSegment(sketch, "E10.0.9.9", {"start": v(12, -9) * mm, "end": v(12, -13) * mm});
            skLineSegment(sketch, "E10.3.9.9", {"start": v(8, -9) * mm, "end": v(12, -9) * mm});
            skLineSegment(sketch, "E10.6.9.9", {"start": v(8, -13) * mm, "end": v(12, -13) * mm});
            skLineSegment(sketch, "E10.9.9.9", {"start": v(8, -9) * mm, "end": v(8, -13) * mm});
            skLineSegment(sketch, "E10.0.9.10", {"start": v(12, -14) * mm, "end": v(12, -18) * mm});
            skLineSegment(sketch, "E10.3.9.10", {"start": v(8, -14) * mm, "end": v(12, -14) * mm});
            skLineSegment(sketch, "E10.6.9.10", {"start": v(8, -18) * mm, "end": v(12, -18) * mm});
            skLineSegment(sketch, "E10.9.9.10", {"start": v(8, -14) * mm, "end": v(8, -18) * mm});
            skLineSegment(sketch, "E10.0.9.11", {"start": v(12, -19) * mm, "end": v(12, -23) * mm});
            skLineSegment(sketch, "E10.3.9.11", {"start": v(8, -19) * mm, "end": v(12, -19) * mm});
            skLineSegment(sketch, "E10.6.9.11", {"start": v(8, -23) * mm, "end": v(12, -23) * mm});
            skLineSegment(sketch, "E10.9.9.11", {"start": v(8, -19) * mm, "end": v(8, -23) * mm});
            skLineSegment(sketch, "E10.0.9.12", {"start": v(12, -24) * mm, "end": v(12, -28) * mm});
            skLineSegment(sketch, "E10.3.9.12", {"start": v(8, -24) * mm, "end": v(12, -24) * mm});
            skLineSegment(sketch, "E10.6.9.12", {"start": v(8, -28) * mm, "end": v(12, -28) * mm});
            skLineSegment(sketch, "E10.9.9.12", {"start": v(8, -24) * mm, "end": v(8, -28) * mm});
            skLineSegment(sketch, "E10.0.9.13", {"start": v(12, -29) * mm, "end": v(12, -33) * mm});
            skLineSegment(sketch, "E10.3.9.13", {"start": v(8, -29) * mm, "end": v(12, -29) * mm});
            skLineSegment(sketch, "E10.6.9.13", {"start": v(8, -33) * mm, "end": v(12, -33) * mm});
            skLineSegment(sketch, "E10.9.9.13", {"start": v(8, -29) * mm, "end": v(8, -33) * mm});
            skLineSegment(sketch, "E10.0.9.14", {"start": v(12, -34) * mm, "end": v(12, -38) * mm});
            skLineSegment(sketch, "E10.3.9.14", {"start": v(8, -34) * mm, "end": v(12, -34) * mm});
            skLineSegment(sketch, "E10.6.9.14", {"start": v(8, -38) * mm, "end": v(12, -38) * mm});
            skLineSegment(sketch, "E10.9.9.14", {"start": v(8, -34) * mm, "end": v(8, -38) * mm});
            skLineSegment(sketch, "E10.0.10.8", {"start": v(17, -4) * mm, "end": v(17, -8) * mm});
            skLineSegment(sketch, "E10.3.10.8", {"start": v(13, -4) * mm, "end": v(17, -4) * mm});
            skLineSegment(sketch, "E10.6.10.8", {"start": v(13, -8) * mm, "end": v(17, -8) * mm});
            skLineSegment(sketch, "E10.9.10.8", {"start": v(13, -4) * mm, "end": v(13, -8) * mm});
            skLineSegment(sketch, "E10.0.10.9", {"start": v(17, -9) * mm, "end": v(17, -13) * mm});
            skLineSegment(sketch, "E10.3.10.9", {"start": v(13, -9) * mm, "end": v(17, -9) * mm});
            skLineSegment(sketch, "E10.6.10.9", {"start": v(13, -13) * mm, "end": v(17, -13) * mm});
            skLineSegment(sketch, "E10.9.10.9", {"start": v(13, -9) * mm, "end": v(13, -13) * mm});
            skLineSegment(sketch, "E10.0.10.10", {"start": v(17, -14) * mm, "end": v(17, -18) * mm});
            skLineSegment(sketch, "E10.3.10.10", {"start": v(13, -14) * mm, "end": v(17, -14) * mm});
            skLineSegment(sketch, "E10.6.10.10", {"start": v(13, -18) * mm, "end": v(17, -18) * mm});
            skLineSegment(sketch, "E10.9.10.10", {"start": v(13, -14) * mm, "end": v(13, -18) * mm});
            skLineSegment(sketch, "E10.0.10.11", {"start": v(17, -19) * mm, "end": v(17, -23) * mm});
            skLineSegment(sketch, "E10.3.10.11", {"start": v(13, -19) * mm, "end": v(17, -19) * mm});
            skLineSegment(sketch, "E10.6.10.11", {"start": v(13, -23) * mm, "end": v(17, -23) * mm});
            skLineSegment(sketch, "E10.9.10.11", {"start": v(13, -19) * mm, "end": v(13, -23) * mm});
            skLineSegment(sketch, "E10.0.10.12", {"start": v(17, -24) * mm, "end": v(17, -28) * mm});
            skLineSegment(sketch, "E10.3.10.12", {"start": v(13, -24) * mm, "end": v(17, -24) * mm});
            skLineSegment(sketch, "E10.6.10.12", {"start": v(13, -28) * mm, "end": v(17, -28) * mm});
            skLineSegment(sketch, "E10.9.10.12", {"start": v(13, -24) * mm, "end": v(13, -28) * mm});
            skLineSegment(sketch, "E10.0.10.13", {"start": v(17, -29) * mm, "end": v(17, -33) * mm});
            skLineSegment(sketch, "E10.3.10.13", {"start": v(13, -29) * mm, "end": v(17, -29) * mm});
            skLineSegment(sketch, "E10.6.10.13", {"start": v(13, -33) * mm, "end": v(17, -33) * mm});
            skLineSegment(sketch, "E10.9.10.13", {"start": v(13, -29) * mm, "end": v(13, -33) * mm});
            skLineSegment(sketch, "E10.0.10.14", {"start": v(17, -34) * mm, "end": v(17, -38) * mm});
            skLineSegment(sketch, "E10.3.10.14", {"start": v(13, -34) * mm, "end": v(17, -34) * mm});
            skLineSegment(sketch, "E10.6.10.14", {"start": v(13, -38) * mm, "end": v(17, -38) * mm});
            skLineSegment(sketch, "E10.9.10.14", {"start": v(13, -34) * mm, "end": v(13, -38) * mm});
            skLineSegment(sketch, "E10.0.11.8", {"start": v(22, -4) * mm, "end": v(22, -8) * mm});
            skLineSegment(sketch, "E10.3.11.8", {"start": v(18, -4) * mm, "end": v(22, -4) * mm});
            skLineSegment(sketch, "E10.6.11.8", {"start": v(18, -8) * mm, "end": v(22, -8) * mm});
            skLineSegment(sketch, "E10.9.11.8", {"start": v(18, -4) * mm, "end": v(18, -8) * mm});
            skLineSegment(sketch, "E10.0.11.9", {"start": v(22, -9) * mm, "end": v(22, -13) * mm});
            skLineSegment(sketch, "E10.3.11.9", {"start": v(18, -9) * mm, "end": v(22, -9) * mm});
            skLineSegment(sketch, "E10.6.11.9", {"start": v(18, -13) * mm, "end": v(22, -13) * mm});
            skLineSegment(sketch, "E10.9.11.9", {"start": v(18, -9) * mm, "end": v(18, -13) * mm});
            skLineSegment(sketch, "E10.0.11.10", {"start": v(22, -14) * mm, "end": v(22, -18) * mm});
            skLineSegment(sketch, "E10.3.11.10", {"start": v(18, -14) * mm, "end": v(22, -14) * mm});
            skLineSegment(sketch, "E10.6.11.10", {"start": v(18, -18) * mm, "end": v(22, -18) * mm});
            skLineSegment(sketch, "E10.9.11.10", {"start": v(18, -14) * mm, "end": v(18, -18) * mm});
            skLineSegment(sketch, "E10.0.11.11", {"start": v(22, -19) * mm, "end": v(22, -23) * mm});
            skLineSegment(sketch, "E10.3.11.11", {"start": v(18, -19) * mm, "end": v(22, -19) * mm});
            skLineSegment(sketch, "E10.6.11.11", {"start": v(18, -23) * mm, "end": v(22, -23) * mm});
            skLineSegment(sketch, "E10.9.11.11", {"start": v(18, -19) * mm, "end": v(18, -23) * mm});
            skLineSegment(sketch, "E10.0.11.12", {"start": v(22, -24) * mm, "end": v(22, -28) * mm});
            skLineSegment(sketch, "E10.3.11.12", {"start": v(18, -24) * mm, "end": v(22, -24) * mm});
            skLineSegment(sketch, "E10.6.11.12", {"start": v(18, -28) * mm, "end": v(22, -28) * mm});
            skLineSegment(sketch, "E10.9.11.12", {"start": v(18, -24) * mm, "end": v(18, -28) * mm});
            skLineSegment(sketch, "E10.0.11.13", {"start": v(22, -29) * mm, "end": v(22, -33) * mm});
            skLineSegment(sketch, "E10.3.11.13", {"start": v(18, -29) * mm, "end": v(22, -29) * mm});
            skLineSegment(sketch, "E10.6.11.13", {"start": v(18, -33) * mm, "end": v(22, -33) * mm});
            skLineSegment(sketch, "E10.9.11.13", {"start": v(18, -29) * mm, "end": v(18, -33) * mm});
            skLineSegment(sketch, "E10.0.11.14", {"start": v(22, -34) * mm, "end": v(22, -38) * mm});
            skLineSegment(sketch, "E10.3.11.14", {"start": v(18, -34) * mm, "end": v(22, -34) * mm});
            skLineSegment(sketch, "E10.6.11.14", {"start": v(18, -38) * mm, "end": v(22, -38) * mm});
            skLineSegment(sketch, "E10.9.11.14", {"start": v(18, -34) * mm, "end": v(18, -38) * mm});
            skLineSegment(sketch, "E10.0.12.8", {"start": v(27, -4) * mm, "end": v(27, -8) * mm});
            skLineSegment(sketch, "E10.3.12.8", {"start": v(23, -4) * mm, "end": v(27, -4) * mm});
            skLineSegment(sketch, "E10.6.12.8", {"start": v(23, -8) * mm, "end": v(27, -8) * mm});
            skLineSegment(sketch, "E10.9.12.8", {"start": v(23, -4) * mm, "end": v(23, -8) * mm});
            skLineSegment(sketch, "E10.0.12.9", {"start": v(27, -9) * mm, "end": v(27, -13) * mm});
            skLineSegment(sketch, "E10.3.12.9", {"start": v(23, -9) * mm, "end": v(27, -9) * mm});
            skLineSegment(sketch, "E10.6.12.9", {"start": v(23, -13) * mm, "end": v(27, -13) * mm});
            skLineSegment(sketch, "E10.9.12.9", {"start": v(23, -9) * mm, "end": v(23, -13) * mm});
            skLineSegment(sketch, "E10.0.12.10", {"start": v(27, -14) * mm, "end": v(27, -18) * mm});
            skLineSegment(sketch, "E10.3.12.10", {"start": v(23, -14) * mm, "end": v(27, -14) * mm});
            skLineSegment(sketch, "E10.6.12.10", {"start": v(23, -18) * mm, "end": v(27, -18) * mm});
            skLineSegment(sketch, "E10.9.12.10", {"start": v(23, -14) * mm, "end": v(23, -18) * mm});
            skLineSegment(sketch, "E10.0.12.11", {"start": v(27, -19) * mm, "end": v(27, -23) * mm});
            skLineSegment(sketch, "E10.3.12.11", {"start": v(23, -19) * mm, "end": v(27, -19) * mm});
            skLineSegment(sketch, "E10.6.12.11", {"start": v(23, -23) * mm, "end": v(27, -23) * mm});
            skLineSegment(sketch, "E10.9.12.11", {"start": v(23, -19) * mm, "end": v(23, -23) * mm});
            skLineSegment(sketch, "E10.0.12.12", {"start": v(27, -24) * mm, "end": v(27, -28) * mm});
            skLineSegment(sketch, "E10.3.12.12", {"start": v(23, -24) * mm, "end": v(27, -24) * mm});
            skLineSegment(sketch, "E10.6.12.12", {"start": v(23, -28) * mm, "end": v(27, -28) * mm});
            skLineSegment(sketch, "E10.9.12.12", {"start": v(23, -24) * mm, "end": v(23, -28) * mm});
            skLineSegment(sketch, "E10.0.12.13", {"start": v(27, -29) * mm, "end": v(27, -33) * mm});
            skLineSegment(sketch, "E10.3.12.13", {"start": v(23, -29) * mm, "end": v(27, -29) * mm});
            skLineSegment(sketch, "E10.6.12.13", {"start": v(23, -33) * mm, "end": v(27, -33) * mm});
            skLineSegment(sketch, "E10.9.12.13", {"start": v(23, -29) * mm, "end": v(23, -33) * mm});
            skLineSegment(sketch, "E10.0.12.14", {"start": v(27, -34) * mm, "end": v(27, -38) * mm});
            skLineSegment(sketch, "E10.3.12.14", {"start": v(23, -34) * mm, "end": v(27, -34) * mm});
            skLineSegment(sketch, "E10.6.12.14", {"start": v(23, -38) * mm, "end": v(27, -38) * mm});
            skLineSegment(sketch, "E10.9.12.14", {"start": v(23, -34) * mm, "end": v(23, -38) * mm});
            skLineSegment(sketch, "E10.0.13.8", {"start": v(32, -4) * mm, "end": v(32, -8) * mm});
            skLineSegment(sketch, "E10.3.13.8", {"start": v(28, -4) * mm, "end": v(32, -4) * mm});
            skLineSegment(sketch, "E10.6.13.8", {"start": v(28, -8) * mm, "end": v(32, -8) * mm});
            skLineSegment(sketch, "E10.9.13.8", {"start": v(28, -4) * mm, "end": v(28, -8) * mm});
            skLineSegment(sketch, "E10.0.13.9", {"start": v(32, -9) * mm, "end": v(32, -13) * mm});
            skLineSegment(sketch, "E10.3.13.9", {"start": v(28, -9) * mm, "end": v(32, -9) * mm});
            skLineSegment(sketch, "E10.6.13.9", {"start": v(28, -13) * mm, "end": v(32, -13) * mm});
            skLineSegment(sketch, "E10.9.13.9", {"start": v(28, -9) * mm, "end": v(28, -13) * mm});
            skLineSegment(sketch, "E10.0.13.10", {"start": v(32, -14) * mm, "end": v(32, -18) * mm});
            skLineSegment(sketch, "E10.3.13.10", {"start": v(28, -14) * mm, "end": v(32, -14) * mm});
            skLineSegment(sketch, "E10.6.13.10", {"start": v(28, -18) * mm, "end": v(32, -18) * mm});
            skLineSegment(sketch, "E10.9.13.10", {"start": v(28, -14) * mm, "end": v(28, -18) * mm});
            skLineSegment(sketch, "E10.0.13.11", {"start": v(32, -19) * mm, "end": v(32, -23) * mm});
            skLineSegment(sketch, "E10.3.13.11", {"start": v(28, -19) * mm, "end": v(32, -19) * mm});
            skLineSegment(sketch, "E10.6.13.11", {"start": v(28, -23) * mm, "end": v(32, -23) * mm});
            skLineSegment(sketch, "E10.9.13.11", {"start": v(28, -19) * mm, "end": v(28, -23) * mm});
            skLineSegment(sketch, "E10.0.13.12", {"start": v(32, -24) * mm, "end": v(32, -28) * mm});
            skLineSegment(sketch, "E10.3.13.12", {"start": v(28, -24) * mm, "end": v(32, -24) * mm});
            skLineSegment(sketch, "E10.6.13.12", {"start": v(28, -28) * mm, "end": v(32, -28) * mm});
            skLineSegment(sketch, "E10.9.13.12", {"start": v(28, -24) * mm, "end": v(28, -28) * mm});
            skLineSegment(sketch, "E10.0.13.13", {"start": v(32, -29) * mm, "end": v(32, -33) * mm});
            skLineSegment(sketch, "E10.3.13.13", {"start": v(28, -29) * mm, "end": v(32, -29) * mm});
            skLineSegment(sketch, "E10.6.13.13", {"start": v(28, -33) * mm, "end": v(32, -33) * mm});
            skLineSegment(sketch, "E10.9.13.13", {"start": v(28, -29) * mm, "end": v(28, -33) * mm});
            skLineSegment(sketch, "E10.0.13.14", {"start": v(32, -34) * mm, "end": v(32, -38) * mm});
            skLineSegment(sketch, "E10.3.13.14", {"start": v(28, -34) * mm, "end": v(32, -34) * mm});
            skLineSegment(sketch, "E10.6.13.14", {"start": v(28, -38) * mm, "end": v(32, -38) * mm});
            skLineSegment(sketch, "E10.9.13.14", {"start": v(28, -34) * mm, "end": v(28, -38) * mm});
            skLineSegment(sketch, "E10.0.14.8", {"start": v(37, -4) * mm, "end": v(37, -8) * mm});
            skLineSegment(sketch, "E10.3.14.8", {"start": v(33, -4) * mm, "end": v(37, -4) * mm});
            skLineSegment(sketch, "E10.6.14.8", {"start": v(33, -8) * mm, "end": v(37, -8) * mm});
            skLineSegment(sketch, "E10.9.14.8", {"start": v(33, -4) * mm, "end": v(33, -8) * mm});
            skLineSegment(sketch, "E10.0.14.9", {"start": v(37, -9) * mm, "end": v(37, -13) * mm});
            skLineSegment(sketch, "E10.3.14.9", {"start": v(33, -9) * mm, "end": v(37, -9) * mm});
            skLineSegment(sketch, "E10.6.14.9", {"start": v(33, -13) * mm, "end": v(37, -13) * mm});
            skLineSegment(sketch, "E10.9.14.9", {"start": v(33, -9) * mm, "end": v(33, -13) * mm});
            skLineSegment(sketch, "E10.0.14.10", {"start": v(37, -14) * mm, "end": v(37, -18) * mm});
            skLineSegment(sketch, "E10.3.14.10", {"start": v(33, -14) * mm, "end": v(37, -14) * mm});
            skLineSegment(sketch, "E10.6.14.10", {"start": v(33, -18) * mm, "end": v(37, -18) * mm});
            skLineSegment(sketch, "E10.9.14.10", {"start": v(33, -14) * mm, "end": v(33, -18) * mm});
            skLineSegment(sketch, "E10.0.14.11", {"start": v(37, -19) * mm, "end": v(37, -23) * mm});
            skLineSegment(sketch, "E10.3.14.11", {"start": v(33, -19) * mm, "end": v(37, -19) * mm});
            skLineSegment(sketch, "E10.6.14.11", {"start": v(33, -23) * mm, "end": v(37, -23) * mm});
            skLineSegment(sketch, "E10.9.14.11", {"start": v(33, -19) * mm, "end": v(33, -23) * mm});
            skLineSegment(sketch, "E10.0.14.12", {"start": v(37, -24) * mm, "end": v(37, -28) * mm});
            skLineSegment(sketch, "E10.3.14.12", {"start": v(33, -24) * mm, "end": v(37, -24) * mm});
            skLineSegment(sketch, "E10.6.14.12", {"start": v(33, -28) * mm, "end": v(37, -28) * mm});
            skLineSegment(sketch, "E10.9.14.12", {"start": v(33, -24) * mm, "end": v(33, -28) * mm});
            skLineSegment(sketch, "E10.0.14.13", {"start": v(37, -29) * mm, "end": v(37, -33) * mm});
            skLineSegment(sketch, "E10.3.14.13", {"start": v(33, -29) * mm, "end": v(37, -29) * mm});
            skLineSegment(sketch, "E10.6.14.13", {"start": v(33, -33) * mm, "end": v(37, -33) * mm});
            skLineSegment(sketch, "E10.9.14.13", {"start": v(33, -29) * mm, "end": v(33, -33) * mm});
            skLineSegment(sketch, "E10.0.14.14", {"start": v(37, -34) * mm, "end": v(37, -38) * mm});
            skLineSegment(sketch, "E10.3.14.14", {"start": v(33, -34) * mm, "end": v(37, -34) * mm});
            skLineSegment(sketch, "E10.6.14.14", {"start": v(33, -38) * mm, "end": v(37, -38) * mm});
            skLineSegment(sketch, "E10.9.14.14", {"start": v(33, -34) * mm, "end": v(33, -38) * mm});
            skSolve(sketch);
        }
        {
            var Q0;
            Q0=makeQuery(id+"F0.imprint","IMPRINT",FACE,{"disambiguationData":[TD([[makeQuery(id+"F0.imprint","IMPRINT",EDGE,{"derivedFrom":sQuery(id+"F0.wireOp",EDGE,"E0.bottom")}),1.0]])]});
            extrude(context, id + "F1", {"entities" : qUnion([Q0]), "depth" : 1.5 * mm, "offsetDistance" : 25 * mm});
        }
        {
            var Q0;
            Q0=makeQuery(id+"F1.opExtrude","SWEPT_EDGE",EDGE,{"disambiguationData":[OSD([sQuery(id+"F0.wireOp",EDGE,"E0.top"),sQuery(id+"F0.wireOp",EDGE,"E0.left")])]});
            var Q1;
            Q1=makeQuery(id+"F1.opExtrude","SWEPT_EDGE",EDGE,{"disambiguationData":[OSD([sQuery(id+"F0.wireOp",EDGE,"E0.bottom"),sQuery(id+"F0.wireOp",EDGE,"E0.left")])]});
            var Q2;
            Q2=makeQuery(id+"F1.opExtrude","SWEPT_EDGE",EDGE,{"disambiguationData":[OSD([sQuery(id+"F0.wireOp",EDGE,"E0.bottom"),sQuery(id+"F0.wireOp",EDGE,"E0.right")])]});
            var Q3;
            Q3=makeQuery(id+"F1.opExtrude","SWEPT_EDGE",EDGE,{"disambiguationData":[OSD([sQuery(id+"F0.wireOp",EDGE,"E0.top"),sQuery(id+"F0.wireOp",EDGE,"E0.right")])]});
            fillet(context, id + "F2", {"entities" : qUnion([Q0, Q1, Q2, Q3]), "radius" : 5 * mm, "tangentPropagation" : true, "allowEdgeOverflow" : false});
        }
        {
            var Q0;
            Q0=makeQuery(id+"F1.opExtrude","CAP_FACE",FACE,{"disambiguationData":[OSD([sQuery(id+"F0.wireOp",EDGE,"E0.bottom"),sQuery(id+"F0.wireOp",EDGE,"E0.top"),sQuery(id+"F0.wireOp",EDGE,"E0.left"),sQuery(id+"F0.wireOp",EDGE,"E0.right"),sQuery(id+"F0.wireOp",EDGE,"E1.bottom"),sQuery(id+"F0.wireOp",EDGE,"E1.top"),sQuery(id+"F0.wireOp",EDGE,"E1.left"),sQuery(id+"F0.wireOp",EDGE,"E1.right"),sQuery(id+"F0.wireOp",EDGE,"E2.0.1.0"),sQuery(id+"F0.wireOp",EDGE,"E2.0.1.1"),sQuery(id+"F0.wireOp",EDGE,"E2.0.1.2"),sQuery(id+"F0.wireOp",EDGE,"E2.0.1.3"),sQuery(id+"F0.wireOp",EDGE,"E2.0.2.0"),sQuery(id+"F0.wireOp",EDGE,"E2.0.2.1"),sQuery(id+"F0.wireOp",EDGE,"E2.0.2.2"),sQuery(id+"F0.wireOp",EDGE,"E2.0.2.3"),sQuery(id+"F0.wireOp",EDGE,"E2.0.3.0"),sQuery(id+"F0.wireOp",EDGE,"E2.0.3.1"),sQuery(id+"F0.wireOp",EDGE,"E2.0.3.2"),sQuery(id+"F0.wireOp",EDGE,"E2.0.3.3"),sQuery(id+"F0.wireOp",EDGE,"E2.0.4.0"),sQuery(id+"F0.wireOp",EDGE,"E2.0.4.1"),sQuery(id+"F0.wireOp",EDGE,"E2.0.4.2"),sQuery(id+"F0.wireOp",EDGE,"E2.0.4.3"),sQuery(id+"F0.wireOp",EDGE,"E2.0.5.0"),sQuery(id+"F0.wireOp",EDGE,"E2.0.5.1"),sQuery(id+"F0.wireOp",EDGE,"E2.0.5.2"),sQuery(id+"F0.wireOp",EDGE,"E2.0.5.3"),sQuery(id+"F0.wireOp",EDGE,"E2.0.6.0"),sQuery(id+"F0.wireOp",EDGE,"E2.0.6.1"),sQuery(id+"F0.wireOp",EDGE,"E2.0.6.2"),sQuery(id+"F0.wireOp",EDGE,"E2.0.6.3"),sQuery(id+"F0.wireOp",EDGE,"E2.0.7.0"),sQuery(id+"F0.wireOp",EDGE,"E2.0.7.1"),sQuery(id+"F0.wireOp",EDGE,"E2.0.7.2"),sQuery(id+"F0.wireOp",EDGE,"E2.0.7.3"),sQuery(id+"F0.wireOp",EDGE,"E2.1.0.0"),sQuery(id+"F0.wireOp",EDGE,"E2.1.0.1"),sQuery(id+"F0.wireOp",EDGE,"E2.1.0.2"),sQuery(id+"F0.wireOp",EDGE,"E2.1.0.3"),sQuery(id+"F0.wireOp",EDGE,"E2.1.1.0"),sQuery(id+"F0.wireOp",EDGE,"E2.1.1.1"),sQuery(id+"F0.wireOp",EDGE,"E2.1.1.2"),sQuery(id+"F0.wireOp",EDGE,"E2.1.1.3"),sQuery(id+"F0.wireOp",EDGE,"E2.1.2.0"),sQuery(id+"F0.wireOp",EDGE,"E2.1.2.1"),sQuery(id+"F0.wireOp",EDGE,"E2.1.2.2"),sQuery(id+"F0.wireOp",EDGE,"E2.1.2.3"),sQuery(id+"F0.wireOp",EDGE,"E2.1.3.0"),sQuery(id+"F0.wireOp",EDGE,"E2.1.3.1"),sQuery(id+"F0.wireOp",EDGE,"E2.1.3.2"),sQuery(id+"F0.wireOp",EDGE,"E2.1.3.3"),sQuery(id+"F0.wireOp",EDGE,"E2.1.4.0"),sQuery(id+"F0.wireOp",EDGE,"E2.1.4.1"),sQuery(id+"F0.wireOp",EDGE,"E2.1.4.2"),sQuery(id+"F0.wireOp",EDGE,"E2.1.4.3"),sQuery(id+"F0.wireOp",EDGE,"E2.1.5.0"),sQuery(id+"F0.wireOp",EDGE,"E2.1.5.1"),sQuery(id+"F0.wireOp",EDGE,"E2.1.5.2"),sQuery(id+"F0.wireOp",EDGE,"E2.1.5.3"),sQuery(id+"F0.wireOp",EDGE,"E2.1.6.0"),sQuery(id+"F0.wireOp",EDGE,"E2.1.6.1"),sQuery(id+"F0.wireOp",EDGE,"E2.1.6.2"),sQuery(id+"F0.wireOp",EDGE,"E2.1.6.3"),sQuery(id+"F0.wireOp",EDGE,"E2.1.7.0"),sQuery(id+"F0.wireOp",EDGE,"E2.1.7.1"),sQuery(id+"F0.wireOp",EDGE,"E2.1.7.2"),sQuery(id+"F0.wireOp",EDGE,"E2.1.7.3"),sQuery(id+"F0.wireOp",EDGE,"E2.2.0.0"),sQuery(id+"F0.wireOp",EDGE,"E2.2.0.1"),sQuery(id+"F0.wireOp",EDGE,"E2.2.0.2"),sQuery(id+"F0.wireOp",EDGE,"E2.2.0.3"),sQuery(id+"F0.wireOp",EDGE,"E2.2.1.0"),sQuery(id+"F0.wireOp",EDGE,"E2.2.1.1"),sQuery(id+"F0.wireOp",EDGE,"E2.2.1.2"),sQuery(id+"F0.wireOp",EDGE,"E2.2.1.3"),sQuery(id+"F0.wireOp",EDGE,"E2.2.2.0"),sQuery(id+"F0.wireOp",EDGE,"E2.2.2.1"),sQuery(id+"F0.wireOp",EDGE,"E2.2.2.2"),sQuery(id+"F0.wireOp",EDGE,"E2.2.2.3"),sQuery(id+"F0.wireOp",EDGE,"E2.2.3.0"),sQuery(id+"F0.wireOp",EDGE,"E2.2.3.1"),sQuery(id+"F0.wireOp",EDGE,"E2.2.3.2"),sQuery(id+"F0.wireOp",EDGE,"E2.2.3.3"),sQuery(id+"F0.wireOp",EDGE,"E2.2.4.0"),sQuery(id+"F0.wireOp",EDGE,"E2.2.4.1"),sQuery(id+"F0.wireOp",EDGE,"E2.2.4.2"),sQuery(id+"F0.wireOp",EDGE,"E2.2.4.3"),sQuery(id+"F0.wireOp",EDGE,"E2.2.5.0"),sQuery(id+"F0.wireOp",EDGE,"E2.2.5.1"),sQuery(id+"F0.wireOp",EDGE,"E2.2.5.2"),sQuery(id+"F0.wireOp",EDGE,"E2.2.5.3"),sQuery(id+"F0.wireOp",EDGE,"E2.2.6.0"),sQuery(id+"F0.wireOp",EDGE,"E2.2.6.1"),sQuery(id+"F0.wireOp",EDGE,"E2.2.6.2"),sQuery(id+"F0.wireOp",EDGE,"E2.2.6.3"),sQuery(id+"F0.wireOp",EDGE,"E2.2.7.0"),sQuery(id+"F0.wireOp",EDGE,"E2.2.7.1"),sQuery(id+"F0.wireOp",EDGE,"E2.2.7.2"),sQuery(id+"F0.wireOp",EDGE,"E2.2.7.3"),sQuery(id+"F0.wireOp",EDGE,"E2.3.0.0"),sQuery(id+"F0.wireOp",EDGE,"E2.3.0.1"),sQuery(id+"F0.wireOp",EDGE,"E2.3.0.2"),sQuery(id+"F0.wireOp",EDGE,"E2.3.0.3"),sQuery(id+"F0.wireOp",EDGE,"E2.3.1.0"),sQuery(id+"F0.wireOp",EDGE,"E2.3.1.1"),sQuery(id+"F0.wireOp",EDGE,"E2.3.1.2"),sQuery(id+"F0.wireOp",EDGE,"E2.3.1.3"),sQuery(id+"F0.wireOp",EDGE,"E2.3.2.0"),sQuery(id+"F0.wireOp",EDGE,"E2.3.2.1"),sQuery(id+"F0.wireOp",EDGE,"E2.3.2.2"),sQuery(id+"F0.wireOp",EDGE,"E2.3.2.3"),sQuery(id+"F0.wireOp",EDGE,"E2.3.3.0"),sQuery(id+"F0.wireOp",EDGE,"E2.3.3.1"),sQuery(id+"F0.wireOp",EDGE,"E2.3.3.2"),sQuery(id+"F0.wireOp",EDGE,"E2.3.3.3"),sQuery(id+"F0.wireOp",EDGE,"E2.3.4.0"),sQuery(id+"F0.wireOp",EDGE,"E2.3.4.1"),sQuery(id+"F0.wireOp",EDGE,"E2.3.4.2"),sQuery(id+"F0.wireOp",EDGE,"E2.3.4.3"),sQuery(id+"F0.wireOp",EDGE,"E2.3.5.0"),sQuery(id+"F0.wireOp",EDGE,"E2.3.5.1"),sQuery(id+"F0.wireOp",EDGE,"E2.3.5.2"),sQuery(id+"F0.wireOp",EDGE,"E2.3.5.3"),sQuery(id+"F0.wireOp",EDGE,"E2.3.6.0"),sQuery(id+"F0.wireOp",EDGE,"E2.3.6.1"),sQuery(id+"F0.wireOp",EDGE,"E2.3.6.2"),sQuery(id+"F0.wireOp",EDGE,"E2.3.6.3"),sQuery(id+"F0.wireOp",EDGE,"E2.3.7.0"),sQuery(id+"F0.wireOp",EDGE,"E2.3.7.1"),sQuery(id+"F0.wireOp",EDGE,"E2.3.7.2"),sQuery(id+"F0.wireOp",EDGE,"E2.3.7.3"),sQuery(id+"F0.wireOp",EDGE,"E2.4.0.0"),sQuery(id+"F0.wireOp",EDGE,"E2.4.0.1"),sQuery(id+"F0.wireOp",EDGE,"E2.4.0.2"),sQuery(id+"F0.wireOp",EDGE,"E2.4.0.3"),sQuery(id+"F0.wireOp",EDGE,"E2.4.1.0"),sQuery(id+"F0.wireOp",EDGE,"E2.4.1.1"),sQuery(id+"F0.wireOp",EDGE,"E2.4.1.2"),sQuery(id+"F0.wireOp",EDGE,"E2.4.1.3"),sQuery(id+"F0.wireOp",EDGE,"E2.4.2.0"),sQuery(id+"F0.wireOp",EDGE,"E2.4.2.1"),sQuery(id+"F0.wireOp",EDGE,"E2.4.2.2"),sQuery(id+"F0.wireOp",EDGE,"E2.4.2.3"),sQuery(id+"F0.wireOp",EDGE,"E2.4.3.0"),sQuery(id+"F0.wireOp",EDGE,"E2.4.3.1"),sQuery(id+"F0.wireOp",EDGE,"E2.4.3.2"),sQuery(id+"F0.wireOp",EDGE,"E2.4.3.3"),sQuery(id+"F0.wireOp",EDGE,"E2.4.4.0"),sQuery(id+"F0.wireOp",EDGE,"E2.4.4.1"),sQuery(id+"F0.wireOp",EDGE,"E2.4.4.2"),sQuery(id+"F0.wireOp",EDGE,"E2.4.4.3"),sQuery(id+"F0.wireOp",EDGE,"E2.4.5.0"),sQuery(id+"F0.wireOp",EDGE,"E2.4.5.1"),sQuery(id+"F0.wireOp",EDGE,"E2.4.5.2"),sQuery(id+"F0.wireOp",EDGE,"E2.4.5.3"),sQuery(id+"F0.wireOp",EDGE,"E2.4.6.0"),sQuery(id+"F0.wireOp",EDGE,"E2.4.6.1"),sQuery(id+"F0.wireOp",EDGE,"E2.4.6.2"),sQuery(id+"F0.wireOp",EDGE,"E2.4.6.3"),sQuery(id+"F0.wireOp",EDGE,"E2.4.7.0"),sQuery(id+"F0.wireOp",EDGE,"E2.4.7.1"),sQuery(id+"F0.wireOp",EDGE,"E2.4.7.2"),sQuery(id+"F0.wireOp",EDGE,"E2.4.7.3"),sQuery(id+"F0.wireOp",EDGE,"E2.5.0.0"),sQuery(id+"F0.wireOp",EDGE,"E2.5.0.1"),sQuery(id+"F0.wireOp",EDGE,"E2.5.0.2"),sQuery(id+"F0.wireOp",EDGE,"E2.5.0.3"),sQuery(id+"F0.wireOp",EDGE,"E2.5.1.0"),sQuery(id+"F0.wireOp",EDGE,"E2.5.1.1"),sQuery(id+"F0.wireOp",EDGE,"E2.5.1.2"),sQuery(id+"F0.wireOp",EDGE,"E2.5.1.3"),sQuery(id+"F0.wireOp",EDGE,"E2.5.2.0"),sQuery(id+"F0.wireOp",EDGE,"E2.5.2.1"),sQuery(id+"F0.wireOp",EDGE,"E2.5.2.2"),sQuery(id+"F0.wireOp",EDGE,"E2.5.2.3"),sQuery(id+"F0.wireOp",EDGE,"E2.5.3.0"),sQuery(id+"F0.wireOp",EDGE,"E2.5.3.1"),sQuery(id+"F0.wireOp",EDGE,"E2.5.3.2"),sQuery(id+"F0.wireOp",EDGE,"E2.5.3.3"),sQuery(id+"F0.wireOp",EDGE,"E2.5.4.0"),sQuery(id+"F0.wireOp",EDGE,"E2.5.4.1"),sQuery(id+"F0.wireOp",EDGE,"E2.5.4.2"),sQuery(id+"F0.wireOp",EDGE,"E2.5.4.3"),sQuery(id+"F0.wireOp",EDGE,"E2.5.5.0"),sQuery(id+"F0.wireOp",EDGE,"E2.5.5.1"),sQuery(id+"F0.wireOp",EDGE,"E2.5.5.2"),sQuery(id+"F0.wireOp",EDGE,"E2.5.5.3"),sQuery(id+"F0.wireOp",EDGE,"E2.5.6.0"),sQuery(id+"F0.wireOp",EDGE,"E2.5.6.1"),sQuery(id+"F0.wireOp",EDGE,"E2.5.6.2"),sQuery(id+"F0.wireOp",EDGE,"E2.5.6.3"),sQuery(id+"F0.wireOp",EDGE,"E2.5.7.0"),sQuery(id+"F0.wireOp",EDGE,"E2.5.7.1"),sQuery(id+"F0.wireOp",EDGE,"E2.5.7.2"),sQuery(id+"F0.wireOp",EDGE,"E2.5.7.3"),sQuery(id+"F0.wireOp",EDGE,"E2.6.0.0"),sQuery(id+"F0.wireOp",EDGE,"E2.6.0.1"),sQuery(id+"F0.wireOp",EDGE,"E2.6.0.2"),sQuery(id+"F0.wireOp",EDGE,"E2.6.0.3"),sQuery(id+"F0.wireOp",EDGE,"E2.6.1.0"),sQuery(id+"F0.wireOp",EDGE,"E2.6.1.1"),sQuery(id+"F0.wireOp",EDGE,"E2.6.1.2"),sQuery(id+"F0.wireOp",EDGE,"E2.6.1.3"),sQuery(id+"F0.wireOp",EDGE,"E2.6.2.0"),sQuery(id+"F0.wireOp",EDGE,"E2.6.2.1"),sQuery(id+"F0.wireOp",EDGE,"E2.6.2.2"),sQuery(id+"F0.wireOp",EDGE,"E2.6.2.3"),sQuery(id+"F0.wireOp",EDGE,"E2.6.3.0"),sQuery(id+"F0.wireOp",EDGE,"E2.6.3.1"),sQuery(id+"F0.wireOp",EDGE,"E2.6.3.2"),sQuery(id+"F0.wireOp",EDGE,"E2.6.3.3"),sQuery(id+"F0.wireOp",EDGE,"E2.6.4.0"),sQuery(id+"F0.wireOp",EDGE,"E2.6.4.1"),sQuery(id+"F0.wireOp",EDGE,"E2.6.4.2"),sQuery(id+"F0.wireOp",EDGE,"E2.6.4.3"),sQuery(id+"F0.wireOp",EDGE,"E2.6.5.0"),sQuery(id+"F0.wireOp",EDGE,"E2.6.5.1"),sQuery(id+"F0.wireOp",EDGE,"E2.6.5.2"),sQuery(id+"F0.wireOp",EDGE,"E2.6.5.3"),sQuery(id+"F0.wireOp",EDGE,"E2.6.6.0"),sQuery(id+"F0.wireOp",EDGE,"E2.6.6.1"),sQuery(id+"F0.wireOp",EDGE,"E2.6.6.2"),sQuery(id+"F0.wireOp",EDGE,"E2.6.6.3"),sQuery(id+"F0.wireOp",EDGE,"E2.6.7.0"),sQuery(id+"F0.wireOp",EDGE,"E2.6.7.1"),sQuery(id+"F0.wireOp",EDGE,"E2.6.7.2"),sQuery(id+"F0.wireOp",EDGE,"E2.6.7.3"),sQuery(id+"F0.wireOp",EDGE,"E2.7.0.0"),sQuery(id+"F0.wireOp",EDGE,"E2.7.0.1"),sQuery(id+"F0.wireOp",EDGE,"E2.7.0.2"),sQuery(id+"F0.wireOp",EDGE,"E2.7.0.3"),sQuery(id+"F0.wireOp",EDGE,"E2.7.1.0"),sQuery(id+"F0.wireOp",EDGE,"E2.7.1.1"),sQuery(id+"F0.wireOp",EDGE,"E2.7.1.2"),sQuery(id+"F0.wireOp",EDGE,"E2.7.1.3"),sQuery(id+"F0.wireOp",EDGE,"E2.7.2.0"),sQuery(id+"F0.wireOp",EDGE,"E2.7.2.1"),sQuery(id+"F0.wireOp",EDGE,"E2.7.2.2"),sQuery(id+"F0.wireOp",EDGE,"E2.7.2.3"),sQuery(id+"F0.wireOp",EDGE,"E2.7.3.0"),sQuery(id+"F0.wireOp",EDGE,"E2.7.3.1"),sQuery(id+"F0.wireOp",EDGE,"E2.7.3.2"),sQuery(id+"F0.wireOp",EDGE,"E2.7.3.3"),sQuery(id+"F0.wireOp",EDGE,"E2.7.4.0"),sQuery(id+"F0.wireOp",EDGE,"E2.7.4.1"),sQuery(id+"F0.wireOp",EDGE,"E2.7.4.2"),sQuery(id+"F0.wireOp",EDGE,"E2.7.4.3"),sQuery(id+"F0.wireOp",EDGE,"E2.7.5.0"),sQuery(id+"F0.wireOp",EDGE,"E2.7.5.1"),sQuery(id+"F0.wireOp",EDGE,"E2.7.5.2"),sQuery(id+"F0.wireOp",EDGE,"E2.7.5.3"),sQuery(id+"F0.wireOp",EDGE,"E2.7.6.0"),sQuery(id+"F0.wireOp",EDGE,"E2.7.6.1"),sQuery(id+"F0.wireOp",EDGE,"E2.7.6.2"),sQuery(id+"F0.wireOp",EDGE,"E2.7.6.3"),sQuery(id+"F0.wireOp",EDGE,"E2.7.7.0"),sQuery(id+"F0.wireOp",EDGE,"E2.7.7.1"),sQuery(id+"F0.wireOp",EDGE,"E2.7.7.2"),sQuery(id+"F0.wireOp",EDGE,"E2.7.7.3"),sQuery(id+"F0.wireOp",EDGE,"E3.0.8.0"),sQuery(id+"F0.wireOp",EDGE,"E3.3.8.0"),sQuery(id+"F0.wireOp",EDGE,"E3.6.8.0"),sQuery(id+"F0.wireOp",EDGE,"E3.9.8.0"),sQuery(id+"F0.wireOp",EDGE,"E3.0.8.1"),sQuery(id+"F0.wireOp",EDGE,"E3.3.8.1"),sQuery(id+"F0.wireOp",EDGE,"E3.6.8.1"),sQuery(id+"F0.wireOp",EDGE,"E3.9.8.1"),sQuery(id+"F0.wireOp",EDGE,"E3.0.8.2"),sQuery(id+"F0.wireOp",EDGE,"E3.3.8.2"),sQuery(id+"F0.wireOp",EDGE,"E3.6.8.2"),sQuery(id+"F0.wireOp",EDGE,"E3.9.8.2"),sQuery(id+"F0.wireOp",EDGE,"E3.0.8.3"),sQuery(id+"F0.wireOp",EDGE,"E3.3.8.3"),sQuery(id+"F0.wireOp",EDGE,"E3.6.8.3"),sQuery(id+"F0.wireOp",EDGE,"E3.9.8.3"),sQuery(id+"F0.wireOp",EDGE,"E3.0.8.4"),sQuery(id+"F0.wireOp",EDGE,"E3.3.8.4"),sQuery(id+"F0.wireOp",EDGE,"E3.6.8.4"),sQuery(id+"F0.wireOp",EDGE,"E3.9.8.4"),sQuery(id+"F0.wireOp",EDGE,"E3.0.8.5"),sQuery(id+"F0.wireOp",EDGE,"E3.3.8.5"),sQuery(id+"F0.wireOp",EDGE,"E3.6.8.5"),sQuery(id+"F0.wireOp",EDGE,"E3.9.8.5"),sQuery(id+"F0.wireOp",EDGE,"E3.0.8.6"),sQuery(id+"F0.wireOp",EDGE,"E3.3.8.6"),sQuery(id+"F0.wireOp",EDGE,"E3.6.8.6"),sQuery(id+"F0.wireOp",EDGE,"E3.9.8.6"),sQuery(id+"F0.wireOp",EDGE,"E3.0.8.7"),sQuery(id+"F0.wireOp",EDGE,"E3.3.8.7"),sQuery(id+"F0.wireOp",EDGE,"E3.6.8.7"),sQuery(id+"F0.wireOp",EDGE,"E3.9.8.7"),sQuery(id+"F0.wireOp",EDGE,"E4.0.9.0"),sQuery(id+"F0.wireOp",EDGE,"E4.3.9.0"),sQuery(id+"F0.wireOp",EDGE,"E4.6.9.0"),sQuery(id+"F0.wireOp",EDGE,"E4.9.9.0"),sQuery(id+"F0.wireOp",EDGE,"E4.0.9.1"),sQuery(id+"F0.wireOp",EDGE,"E4.3.9.1"),sQuery(id+"F0.wireOp",EDGE,"E4.6.9.1"),sQuery(id+"F0.wireOp",EDGE,"E4.9.9.1"),sQuery(id+"F0.wireOp",EDGE,"E4.0.9.2"),sQuery(id+"F0.wireOp",EDGE,"E4.3.9.2"),sQuery(id+"F0.wireOp",EDGE,"E4.6.9.2"),sQuery(id+"F0.wireOp",EDGE,"E4.9.9.2"),sQuery(id+"F0.wireOp",EDGE,"E4.0.9.3"),sQuery(id+"F0.wireOp",EDGE,"E4.3.9.3"),sQuery(id+"F0.wireOp",EDGE,"E4.6.9.3"),sQuery(id+"F0.wireOp",EDGE,"E4.9.9.3"),sQuery(id+"F0.wireOp",EDGE,"E4.0.9.4"),sQuery(id+"F0.wireOp",EDGE,"E4.3.9.4"),sQuery(id+"F0.wireOp",EDGE,"E4.6.9.4"),sQuery(id+"F0.wireOp",EDGE,"E4.9.9.4"),sQuery(id+"F0.wireOp",EDGE,"E4.0.9.5"),sQuery(id+"F0.wireOp",EDGE,"E4.3.9.5"),sQuery(id+"F0.wireOp",EDGE,"E4.6.9.5"),sQuery(id+"F0.wireOp",EDGE,"E4.9.9.5"),sQuery(id+"F0.wireOp",EDGE,"E4.0.9.6"),sQuery(id+"F0.wireOp",EDGE,"E4.3.9.6"),sQuery(id+"F0.wireOp",EDGE,"E4.6.9.6"),sQuery(id+"F0.wireOp",EDGE,"E4.9.9.6"),sQuery(id+"F0.wireOp",EDGE,"E4.0.9.7"),sQuery(id+"F0.wireOp",EDGE,"E4.3.9.7"),sQuery(id+"F0.wireOp",EDGE,"E4.6.9.7"),sQuery(id+"F0.wireOp",EDGE,"E4.9.9.7"),sQuery(id+"F0.wireOp",EDGE,"E5.0.10.0"),sQuery(id+"F0.wireOp",EDGE,"E5.3.10.0"),sQuery(id+"F0.wireOp",EDGE,"E5.6.10.0"),sQuery(id+"F0.wireOp",EDGE,"E5.9.10.0"),sQuery(id+"F0.wireOp",EDGE,"E5.0.10.1"),sQuery(id+"F0.wireOp",EDGE,"E5.3.10.1"),sQuery(id+"F0.wireOp",EDGE,"E5.6.10.1"),sQuery(id+"F0.wireOp",EDGE,"E5.9.10.1"),sQuery(id+"F0.wireOp",EDGE,"E5.0.10.2"),sQuery(id+"F0.wireOp",EDGE,"E5.3.10.2"),sQuery(id+"F0.wireOp",EDGE,"E5.6.10.2"),sQuery(id+"F0.wireOp",EDGE,"E5.9.10.2"),sQuery(id+"F0.wireOp",EDGE,"E5.0.10.3"),sQuery(id+"F0.wireOp",EDGE,"E5.3.10.3"),sQuery(id+"F0.wireOp",EDGE,"E5.6.10.3"),sQuery(id+"F0.wireOp",EDGE,"E5.9.10.3"),sQuery(id+"F0.wireOp",EDGE,"E5.0.10.4"),sQuery(id+"F0.wireOp",EDGE,"E5.3.10.4"),sQuery(id+"F0.wireOp",EDGE,"E5.6.10.4"),sQuery(id+"F0.wireOp",EDGE,"E5.9.10.4"),sQuery(id+"F0.wireOp",EDGE,"E5.0.10.5"),sQuery(id+"F0.wireOp",EDGE,"E5.3.10.5"),sQuery(id+"F0.wireOp",EDGE,"E5.6.10.5"),sQuery(id+"F0.wireOp",EDGE,"E5.9.10.5"),sQuery(id+"F0.wireOp",EDGE,"E5.0.10.6"),sQuery(id+"F0.wireOp",EDGE,"E5.3.10.6"),sQuery(id+"F0.wireOp",EDGE,"E5.6.10.6"),sQuery(id+"F0.wireOp",EDGE,"E5.9.10.6"),sQuery(id+"F0.wireOp",EDGE,"E5.0.10.7"),sQuery(id+"F0.wireOp",EDGE,"E5.3.10.7"),sQuery(id+"F0.wireOp",EDGE,"E5.6.10.7"),sQuery(id+"F0.wireOp",EDGE,"E5.9.10.7"),sQuery(id+"F0.wireOp",EDGE,"E6.0.11.0"),sQuery(id+"F0.wireOp",EDGE,"E6.3.11.0"),sQuery(id+"F0.wireOp",EDGE,"E6.6.11.0"),sQuery(id+"F0.wireOp",EDGE,"E6.9.11.0"),sQuery(id+"F0.wireOp",EDGE,"E6.0.11.1"),sQuery(id+"F0.wireOp",EDGE,"E6.3.11.1"),sQuery(id+"F0.wireOp",EDGE,"E6.6.11.1"),sQuery(id+"F0.wireOp",EDGE,"E6.9.11.1"),sQuery(id+"F0.wireOp",EDGE,"E6.0.11.2"),sQuery(id+"F0.wireOp",EDGE,"E6.3.11.2"),sQuery(id+"F0.wireOp",EDGE,"E6.6.11.2"),sQuery(id+"F0.wireOp",EDGE,"E6.9.11.2"),sQuery(id+"F0.wireOp",EDGE,"E6.0.11.3"),sQuery(id+"F0.wireOp",EDGE,"E6.3.11.3"),sQuery(id+"F0.wireOp",EDGE,"E6.6.11.3"),sQuery(id+"F0.wireOp",EDGE,"E6.9.11.3"),sQuery(id+"F0.wireOp",EDGE,"E6.0.11.4"),sQuery(id+"F0.wireOp",EDGE,"E6.3.11.4"),sQuery(id+"F0.wireOp",EDGE,"E6.6.11.4"),sQuery(id+"F0.wireOp",EDGE,"E6.9.11.4"),sQuery(id+"F0.wireOp",EDGE,"E6.0.11.5"),sQuery(id+"F0.wireOp",EDGE,"E6.3.11.5"),sQuery(id+"F0.wireOp",EDGE,"E6.6.11.5"),sQuery(id+"F0.wireOp",EDGE,"E6.9.11.5"),sQuery(id+"F0.wireOp",EDGE,"E6.0.11.6"),sQuery(id+"F0.wireOp",EDGE,"E6.3.11.6"),sQuery(id+"F0.wireOp",EDGE,"E6.6.11.6"),sQuery(id+"F0.wireOp",EDGE,"E6.9.11.6"),sQuery(id+"F0.wireOp",EDGE,"E6.0.11.7"),sQuery(id+"F0.wireOp",EDGE,"E6.3.11.7"),sQuery(id+"F0.wireOp",EDGE,"E6.6.11.7"),sQuery(id+"F0.wireOp",EDGE,"E6.9.11.7"),sQuery(id+"F0.wireOp",EDGE,"E7.0.12.0"),sQuery(id+"F0.wireOp",EDGE,"E7.3.12.0"),sQuery(id+"F0.wireOp",EDGE,"E7.6.12.0"),sQuery(id+"F0.wireOp",EDGE,"E7.9.12.0"),sQuery(id+"F0.wireOp",EDGE,"E7.0.12.1"),sQuery(id+"F0.wireOp",EDGE,"E7.3.12.1"),sQuery(id+"F0.wireOp",EDGE,"E7.6.12.1"),sQuery(id+"F0.wireOp",EDGE,"E7.9.12.1"),sQuery(id+"F0.wireOp",EDGE,"E7.0.12.2"),sQuery(id+"F0.wireOp",EDGE,"E7.3.12.2"),sQuery(id+"F0.wireOp",EDGE,"E7.6.12.2"),sQuery(id+"F0.wireOp",EDGE,"E7.9.12.2"),sQuery(id+"F0.wireOp",EDGE,"E7.0.12.3"),sQuery(id+"F0.wireOp",EDGE,"E7.3.12.3"),sQuery(id+"F0.wireOp",EDGE,"E7.6.12.3"),sQuery(id+"F0.wireOp",EDGE,"E7.9.12.3"),sQuery(id+"F0.wireOp",EDGE,"E7.0.12.4"),sQuery(id+"F0.wireOp",EDGE,"E7.3.12.4"),sQuery(id+"F0.wireOp",EDGE,"E7.6.12.4"),sQuery(id+"F0.wireOp",EDGE,"E7.9.12.4"),sQuery(id+"F0.wireOp",EDGE,"E7.0.12.5"),sQuery(id+"F0.wireOp",EDGE,"E7.3.12.5"),sQuery(id+"F0.wireOp",EDGE,"E7.6.12.5"),sQuery(id+"F0.wireOp",EDGE,"E7.9.12.5"),sQuery(id+"F0.wireOp",EDGE,"E7.0.12.6"),sQuery(id+"F0.wireOp",EDGE,"E7.3.12.6"),sQuery(id+"F0.wireOp",EDGE,"E7.6.12.6"),sQuery(id+"F0.wireOp",EDGE,"E7.9.12.6"),sQuery(id+"F0.wireOp",EDGE,"E7.0.12.7"),sQuery(id+"F0.wireOp",EDGE,"E7.3.12.7"),sQuery(id+"F0.wireOp",EDGE,"E7.6.12.7"),sQuery(id+"F0.wireOp",EDGE,"E7.9.12.7"),sQuery(id+"F0.wireOp",EDGE,"E8.0.13.0"),sQuery(id+"F0.wireOp",EDGE,"E8.3.13.0"),sQuery(id+"F0.wireOp",EDGE,"E8.6.13.0"),sQuery(id+"F0.wireOp",EDGE,"E8.9.13.0"),sQuery(id+"F0.wireOp",EDGE,"E8.0.13.1"),sQuery(id+"F0.wireOp",EDGE,"E8.3.13.1"),sQuery(id+"F0.wireOp",EDGE,"E8.6.13.1"),sQuery(id+"F0.wireOp",EDGE,"E8.9.13.1"),sQuery(id+"F0.wireOp",EDGE,"E8.0.13.2"),sQuery(id+"F0.wireOp",EDGE,"E8.3.13.2"),sQuery(id+"F0.wireOp",EDGE,"E8.6.13.2"),sQuery(id+"F0.wireOp",EDGE,"E8.9.13.2"),sQuery(id+"F0.wireOp",EDGE,"E8.0.13.3"),sQuery(id+"F0.wireOp",EDGE,"E8.3.13.3"),sQuery(id+"F0.wireOp",EDGE,"E8.6.13.3"),sQuery(id+"F0.wireOp",EDGE,"E8.9.13.3"),sQuery(id+"F0.wireOp",EDGE,"E8.0.13.4"),sQuery(id+"F0.wireOp",EDGE,"E8.3.13.4"),sQuery(id+"F0.wireOp",EDGE,"E8.6.13.4"),sQuery(id+"F0.wireOp",EDGE,"E8.9.13.4"),sQuery(id+"F0.wireOp",EDGE,"E8.0.13.5"),sQuery(id+"F0.wireOp",EDGE,"E8.3.13.5"),sQuery(id+"F0.wireOp",EDGE,"E8.6.13.5"),sQuery(id+"F0.wireOp",EDGE,"E8.9.13.5"),sQuery(id+"F0.wireOp",EDGE,"E8.0.13.6"),sQuery(id+"F0.wireOp",EDGE,"E8.3.13.6"),sQuery(id+"F0.wireOp",EDGE,"E8.6.13.6"),sQuery(id+"F0.wireOp",EDGE,"E8.9.13.6"),sQuery(id+"F0.wireOp",EDGE,"E8.0.13.7"),sQuery(id+"F0.wireOp",EDGE,"E8.3.13.7"),sQuery(id+"F0.wireOp",EDGE,"E8.6.13.7"),sQuery(id+"F0.wireOp",EDGE,"E8.9.13.7"),sQuery(id+"F0.wireOp",EDGE,"E9.0.14.0"),sQuery(id+"F0.wireOp",EDGE,"E9.3.14.0"),sQuery(id+"F0.wireOp",EDGE,"E9.6.14.0"),sQuery(id+"F0.wireOp",EDGE,"E9.9.14.0"),sQuery(id+"F0.wireOp",EDGE,"E9.0.14.1"),sQuery(id+"F0.wireOp",EDGE,"E9.3.14.1"),sQuery(id+"F0.wireOp",EDGE,"E9.6.14.1"),sQuery(id+"F0.wireOp",EDGE,"E9.9.14.1"),sQuery(id+"F0.wireOp",EDGE,"E9.0.14.2"),sQuery(id+"F0.wireOp",EDGE,"E9.3.14.2"),sQuery(id+"F0.wireOp",EDGE,"E9.6.14.2"),sQuery(id+"F0.wireOp",EDGE,"E9.9.14.2"),sQuery(id+"F0.wireOp",EDGE,"E9.0.14.3"),sQuery(id+"F0.wireOp",EDGE,"E9.3.14.3"),sQuery(id+"F0.wireOp",EDGE,"E9.6.14.3"),sQuery(id+"F0.wireOp",EDGE,"E9.9.14.3"),sQuery(id+"F0.wireOp",EDGE,"E9.0.14.4"),sQuery(id+"F0.wireOp",EDGE,"E9.3.14.4"),sQuery(id+"F0.wireOp",EDGE,"E9.6.14.4"),sQuery(id+"F0.wireOp",EDGE,"E9.9.14.4"),sQuery(id+"F0.wireOp",EDGE,"E9.0.14.5"),sQuery(id+"F0.wireOp",EDGE,"E9.3.14.5"),sQuery(id+"F0.wireOp",EDGE,"E9.6.14.5"),sQuery(id+"F0.wireOp",EDGE,"E9.9.14.5"),sQuery(id+"F0.wireOp",EDGE,"E9.0.14.6"),sQuery(id+"F0.wireOp",EDGE,"E9.3.14.6"),sQuery(id+"F0.wireOp",EDGE,"E9.6.14.6"),sQuery(id+"F0.wireOp",EDGE,"E9.9.14.6"),sQuery(id+"F0.wireOp",EDGE,"E9.0.14.7"),sQuery(id+"F0.wireOp",EDGE,"E9.3.14.7"),sQuery(id+"F0.wireOp",EDGE,"E9.6.14.7"),sQuery(id+"F0.wireOp",EDGE,"E9.9.14.7"),sQuery(id+"F0.wireOp",EDGE,"E10.0.0.8"),sQuery(id+"F0.wireOp",EDGE,"E10.3.0.8"),sQuery(id+"F0.wireOp",EDGE,"E10.6.0.8"),sQuery(id+"F0.wireOp",EDGE,"E10.9.0.8"),sQuery(id+"F0.wireOp",EDGE,"E10.0.0.9"),sQuery(id+"F0.wireOp",EDGE,"E10.3.0.9"),sQuery(id+"F0.wireOp",EDGE,"E10.6.0.9"),sQuery(id+"F0.wireOp",EDGE,"E10.9.0.9"),sQuery(id+"F0.wireOp",EDGE,"E10.0.0.10"),sQuery(id+"F0.wireOp",EDGE,"E10.3.0.10"),sQuery(id+"F0.wireOp",EDGE,"E10.6.0.10"),sQuery(id+"F0.wireOp",EDGE,"E10.9.0.10"),sQuery(id+"F0.wireOp",EDGE,"E10.0.0.11"),sQuery(id+"F0.wireOp",EDGE,"E10.3.0.11"),sQuery(id+"F0.wireOp",EDGE,"E10.6.0.11"),sQuery(id+"F0.wireOp",EDGE,"E10.9.0.11"),sQuery(id+"F0.wireOp",EDGE,"E10.0.0.12"),sQuery(id+"F0.wireOp",EDGE,"E10.3.0.12"),sQuery(id+"F0.wireOp",EDGE,"E10.6.0.12"),sQuery(id+"F0.wireOp",EDGE,"E10.9.0.12"),sQuery(id+"F0.wireOp",EDGE,"E10.0.0.13"),sQuery(id+"F0.wireOp",EDGE,"E10.3.0.13"),sQuery(id+"F0.wireOp",EDGE,"E10.6.0.13"),sQuery(id+"F0.wireOp",EDGE,"E10.9.0.13"),sQuery(id+"F0.wireOp",EDGE,"E10.0.0.14"),sQuery(id+"F0.wireOp",EDGE,"E10.3.0.14"),sQuery(id+"F0.wireOp",EDGE,"E10.6.0.14"),sQuery(id+"F0.wireOp",EDGE,"E10.9.0.14"),sQuery(id+"F0.wireOp",EDGE,"E10.0.1.8"),sQuery(id+"F0.wireOp",EDGE,"E10.3.1.8"),sQuery(id+"F0.wireOp",EDGE,"E10.6.1.8"),sQuery(id+"F0.wireOp",EDGE,"E10.9.1.8"),sQuery(id+"F0.wireOp",EDGE,"E10.0.1.9"),sQuery(id+"F0.wireOp",EDGE,"E10.3.1.9"),sQuery(id+"F0.wireOp",EDGE,"E10.6.1.9"),sQuery(id+"F0.wireOp",EDGE,"E10.9.1.9"),sQuery(id+"F0.wireOp",EDGE,"E10.0.1.10"),sQuery(id+"F0.wireOp",EDGE,"E10.3.1.10"),sQuery(id+"F0.wireOp",EDGE,"E10.6.1.10"),sQuery(id+"F0.wireOp",EDGE,"E10.9.1.10"),sQuery(id+"F0.wireOp",EDGE,"E10.0.1.11"),sQuery(id+"F0.wireOp",EDGE,"E10.3.1.11"),sQuery(id+"F0.wireOp",EDGE,"E10.6.1.11"),sQuery(id+"F0.wireOp",EDGE,"E10.9.1.11"),sQuery(id+"F0.wireOp",EDGE,"E10.0.1.12"),sQuery(id+"F0.wireOp",EDGE,"E10.3.1.12"),sQuery(id+"F0.wireOp",EDGE,"E10.6.1.12"),sQuery(id+"F0.wireOp",EDGE,"E10.9.1.12"),sQuery(id+"F0.wireOp",EDGE,"E10.0.1.13"),sQuery(id+"F0.wireOp",EDGE,"E10.3.1.13"),sQuery(id+"F0.wireOp",EDGE,"E10.6.1.13"),sQuery(id+"F0.wireOp",EDGE,"E10.9.1.13"),sQuery(id+"F0.wireOp",EDGE,"E10.0.1.14"),sQuery(id+"F0.wireOp",EDGE,"E10.3.1.14"),sQuery(id+"F0.wireOp",EDGE,"E10.6.1.14"),sQuery(id+"F0.wireOp",EDGE,"E10.9.1.14"),sQuery(id+"F0.wireOp",EDGE,"E10.0.2.8"),sQuery(id+"F0.wireOp",EDGE,"E10.3.2.8"),sQuery(id+"F0.wireOp",EDGE,"E10.6.2.8"),sQuery(id+"F0.wireOp",EDGE,"E10.9.2.8"),sQuery(id+"F0.wireOp",EDGE,"E10.0.2.9"),sQuery(id+"F0.wireOp",EDGE,"E10.3.2.9"),sQuery(id+"F0.wireOp",EDGE,"E10.6.2.9"),sQuery(id+"F0.wireOp",EDGE,"E10.9.2.9"),sQuery(id+"F0.wireOp",EDGE,"E10.0.2.10"),sQuery(id+"F0.wireOp",EDGE,"E10.3.2.10"),sQuery(id+"F0.wireOp",EDGE,"E10.6.2.10"),sQuery(id+"F0.wireOp",EDGE,"E10.9.2.10"),sQuery(id+"F0.wireOp",EDGE,"E10.0.2.11"),sQuery(id+"F0.wireOp",EDGE,"E10.3.2.11"),sQuery(id+"F0.wireOp",EDGE,"E10.6.2.11"),sQuery(id+"F0.wireOp",EDGE,"E10.9.2.11"),sQuery(id+"F0.wireOp",EDGE,"E10.0.2.12"),sQuery(id+"F0.wireOp",EDGE,"E10.3.2.12"),sQuery(id+"F0.wireOp",EDGE,"E10.6.2.12"),sQuery(id+"F0.wireOp",EDGE,"E10.9.2.12"),sQuery(id+"F0.wireOp",EDGE,"E10.0.2.13"),sQuery(id+"F0.wireOp",EDGE,"E10.3.2.13"),sQuery(id+"F0.wireOp",EDGE,"E10.6.2.13"),sQuery(id+"F0.wireOp",EDGE,"E10.9.2.13"),sQuery(id+"F0.wireOp",EDGE,"E10.0.2.14"),sQuery(id+"F0.wireOp",EDGE,"E10.3.2.14"),sQuery(id+"F0.wireOp",EDGE,"E10.6.2.14"),sQuery(id+"F0.wireOp",EDGE,"E10.9.2.14"),sQuery(id+"F0.wireOp",EDGE,"E10.0.3.8"),sQuery(id+"F0.wireOp",EDGE,"E10.3.3.8"),sQuery(id+"F0.wireOp",EDGE,"E10.6.3.8"),sQuery(id+"F0.wireOp",EDGE,"E10.9.3.8"),sQuery(id+"F0.wireOp",EDGE,"E10.0.3.9"),sQuery(id+"F0.wireOp",EDGE,"E10.3.3.9"),sQuery(id+"F0.wireOp",EDGE,"E10.6.3.9"),sQuery(id+"F0.wireOp",EDGE,"E10.9.3.9"),sQuery(id+"F0.wireOp",EDGE,"E10.0.3.10"),sQuery(id+"F0.wireOp",EDGE,"E10.3.3.10"),sQuery(id+"F0.wireOp",EDGE,"E10.6.3.10"),sQuery(id+"F0.wireOp",EDGE,"E10.9.3.10"),sQuery(id+"F0.wireOp",EDGE,"E10.0.3.11"),sQuery(id+"F0.wireOp",EDGE,"E10.3.3.11"),sQuery(id+"F0.wireOp",EDGE,"E10.6.3.11"),sQuery(id+"F0.wireOp",EDGE,"E10.9.3.11"),sQuery(id+"F0.wireOp",EDGE,"E10.0.3.12"),sQuery(id+"F0.wireOp",EDGE,"E10.3.3.12"),sQuery(id+"F0.wireOp",EDGE,"E10.6.3.12"),sQuery(id+"F0.wireOp",EDGE,"E10.9.3.12"),sQuery(id+"F0.wireOp",EDGE,"E10.0.3.13"),sQuery(id+"F0.wireOp",EDGE,"E10.3.3.13"),sQuery(id+"F0.wireOp",EDGE,"E10.6.3.13"),sQuery(id+"F0.wireOp",EDGE,"E10.9.3.13"),sQuery(id+"F0.wireOp",EDGE,"E10.0.3.14"),sQuery(id+"F0.wireOp",EDGE,"E10.3.3.14"),sQuery(id+"F0.wireOp",EDGE,"E10.6.3.14"),sQuery(id+"F0.wireOp",EDGE,"E10.9.3.14"),sQuery(id+"F0.wireOp",EDGE,"E10.0.4.8"),sQuery(id+"F0.wireOp",EDGE,"E10.3.4.8"),sQuery(id+"F0.wireOp",EDGE,"E10.6.4.8"),sQuery(id+"F0.wireOp",EDGE,"E10.9.4.8"),sQuery(id+"F0.wireOp",EDGE,"E10.0.4.9"),sQuery(id+"F0.wireOp",EDGE,"E10.3.4.9"),sQuery(id+"F0.wireOp",EDGE,"E10.6.4.9"),sQuery(id+"F0.wireOp",EDGE,"E10.9.4.9"),sQuery(id+"F0.wireOp",EDGE,"E10.0.4.10"),sQuery(id+"F0.wireOp",EDGE,"E10.3.4.10"),sQuery(id+"F0.wireOp",EDGE,"E10.6.4.10"),sQuery(id+"F0.wireOp",EDGE,"E10.9.4.10"),sQuery(id+"F0.wireOp",EDGE,"E10.0.4.11"),sQuery(id+"F0.wireOp",EDGE,"E10.3.4.11"),sQuery(id+"F0.wireOp",EDGE,"E10.6.4.11"),sQuery(id+"F0.wireOp",EDGE,"E10.9.4.11"),sQuery(id+"F0.wireOp",EDGE,"E10.0.4.12"),sQuery(id+"F0.wireOp",EDGE,"E10.3.4.12"),sQuery(id+"F0.wireOp",EDGE,"E10.6.4.12"),sQuery(id+"F0.wireOp",EDGE,"E10.9.4.12"),sQuery(id+"F0.wireOp",EDGE,"E10.0.4.13"),sQuery(id+"F0.wireOp",EDGE,"E10.3.4.13"),sQuery(id+"F0.wireOp",EDGE,"E10.6.4.13"),sQuery(id+"F0.wireOp",EDGE,"E10.9.4.13"),sQuery(id+"F0.wireOp",EDGE,"E10.0.4.14"),sQuery(id+"F0.wireOp",EDGE,"E10.3.4.14"),sQuery(id+"F0.wireOp",EDGE,"E10.6.4.14"),sQuery(id+"F0.wireOp",EDGE,"E10.9.4.14"),sQuery(id+"F0.wireOp",EDGE,"E10.0.5.8"),sQuery(id+"F0.wireOp",EDGE,"E10.3.5.8"),sQuery(id+"F0.wireOp",EDGE,"E10.6.5.8"),sQuery(id+"F0.wireOp",EDGE,"E10.9.5.8"),sQuery(id+"F0.wireOp",EDGE,"E10.0.5.9"),sQuery(id+"F0.wireOp",EDGE,"E10.3.5.9"),sQuery(id+"F0.wireOp",EDGE,"E10.6.5.9"),sQuery(id+"F0.wireOp",EDGE,"E10.9.5.9"),sQuery(id+"F0.wireOp",EDGE,"E10.0.5.10"),sQuery(id+"F0.wireOp",EDGE,"E10.3.5.10"),sQuery(id+"F0.wireOp",EDGE,"E10.6.5.10"),sQuery(id+"F0.wireOp",EDGE,"E10.9.5.10"),sQuery(id+"F0.wireOp",EDGE,"E10.0.5.11"),sQuery(id+"F0.wireOp",EDGE,"E10.3.5.11"),sQuery(id+"F0.wireOp",EDGE,"E10.6.5.11"),sQuery(id+"F0.wireOp",EDGE,"E10.9.5.11"),sQuery(id+"F0.wireOp",EDGE,"E10.0.5.12"),sQuery(id+"F0.wireOp",EDGE,"E10.3.5.12"),sQuery(id+"F0.wireOp",EDGE,"E10.6.5.12"),sQuery(id+"F0.wireOp",EDGE,"E10.9.5.12"),sQuery(id+"F0.wireOp",EDGE,"E10.0.5.13"),sQuery(id+"F0.wireOp",EDGE,"E10.3.5.13"),sQuery(id+"F0.wireOp",EDGE,"E10.6.5.13"),sQuery(id+"F0.wireOp",EDGE,"E10.9.5.13"),sQuery(id+"F0.wireOp",EDGE,"E10.0.5.14"),sQuery(id+"F0.wireOp",EDGE,"E10.3.5.14"),sQuery(id+"F0.wireOp",EDGE,"E10.6.5.14"),sQuery(id+"F0.wireOp",EDGE,"E10.9.5.14"),sQuery(id+"F0.wireOp",EDGE,"E10.0.6.8"),sQuery(id+"F0.wireOp",EDGE,"E10.3.6.8"),sQuery(id+"F0.wireOp",EDGE,"E10.6.6.8"),sQuery(id+"F0.wireOp",EDGE,"E10.9.6.8"),sQuery(id+"F0.wireOp",EDGE,"E10.0.6.9"),sQuery(id+"F0.wireOp",EDGE,"E10.3.6.9"),sQuery(id+"F0.wireOp",EDGE,"E10.6.6.9"),sQuery(id+"F0.wireOp",EDGE,"E10.9.6.9"),sQuery(id+"F0.wireOp",EDGE,"E10.0.6.10"),sQuery(id+"F0.wireOp",EDGE,"E10.3.6.10"),sQuery(id+"F0.wireOp",EDGE,"E10.6.6.10"),sQuery(id+"F0.wireOp",EDGE,"E10.9.6.10"),sQuery(id+"F0.wireOp",EDGE,"E10.0.6.11"),sQuery(id+"F0.wireOp",EDGE,"E10.3.6.11"),sQuery(id+"F0.wireOp",EDGE,"E10.6.6.11"),sQuery(id+"F0.wireOp",EDGE,"E10.9.6.11"),sQuery(id+"F0.wireOp",EDGE,"E10.0.6.12"),sQuery(id+"F0.wireOp",EDGE,"E10.3.6.12"),sQuery(id+"F0.wireOp",EDGE,"E10.6.6.12"),sQuery(id+"F0.wireOp",EDGE,"E10.9.6.12"),sQuery(id+"F0.wireOp",EDGE,"E10.0.6.13"),sQuery(id+"F0.wireOp",EDGE,"E10.3.6.13"),sQuery(id+"F0.wireOp",EDGE,"E10.6.6.13"),sQuery(id+"F0.wireOp",EDGE,"E10.9.6.13"),sQuery(id+"F0.wireOp",EDGE,"E10.0.6.14"),sQuery(id+"F0.wireOp",EDGE,"E10.3.6.14"),sQuery(id+"F0.wireOp",EDGE,"E10.6.6.14"),sQuery(id+"F0.wireOp",EDGE,"E10.9.6.14"),sQuery(id+"F0.wireOp",EDGE,"E10.0.7.8"),sQuery(id+"F0.wireOp",EDGE,"E10.3.7.8"),sQuery(id+"F0.wireOp",EDGE,"E10.6.7.8"),sQuery(id+"F0.wireOp",EDGE,"E10.9.7.8"),sQuery(id+"F0.wireOp",EDGE,"E10.0.7.9"),sQuery(id+"F0.wireOp",EDGE,"E10.3.7.9"),sQuery(id+"F0.wireOp",EDGE,"E10.6.7.9"),sQuery(id+"F0.wireOp",EDGE,"E10.9.7.9"),sQuery(id+"F0.wireOp",EDGE,"E10.0.7.10"),sQuery(id+"F0.wireOp",EDGE,"E10.3.7.10"),sQuery(id+"F0.wireOp",EDGE,"E10.6.7.10"),sQuery(id+"F0.wireOp",EDGE,"E10.9.7.10"),sQuery(id+"F0.wireOp",EDGE,"E10.0.7.11"),sQuery(id+"F0.wireOp",EDGE,"E10.3.7.11"),sQuery(id+"F0.wireOp",EDGE,"E10.6.7.11"),sQuery(id+"F0.wireOp",EDGE,"E10.9.7.11"),sQuery(id+"F0.wireOp",EDGE,"E10.0.7.12"),sQuery(id+"F0.wireOp",EDGE,"E10.3.7.12"),sQuery(id+"F0.wireOp",EDGE,"E10.6.7.12"),sQuery(id+"F0.wireOp",EDGE,"E10.9.7.12"),sQuery(id+"F0.wireOp",EDGE,"E10.0.7.13"),sQuery(id+"F0.wireOp",EDGE,"E10.3.7.13"),sQuery(id+"F0.wireOp",EDGE,"E10.6.7.13"),sQuery(id+"F0.wireOp",EDGE,"E10.9.7.13"),sQuery(id+"F0.wireOp",EDGE,"E10.0.7.14"),sQuery(id+"F0.wireOp",EDGE,"E10.3.7.14"),sQuery(id+"F0.wireOp",EDGE,"E10.6.7.14"),sQuery(id+"F0.wireOp",EDGE,"E10.9.7.14"),sQuery(id+"F0.wireOp",EDGE,"E10.0.8.8"),sQuery(id+"F0.wireOp",EDGE,"E10.3.8.8"),sQuery(id+"F0.wireOp",EDGE,"E10.6.8.8"),sQuery(id+"F0.wireOp",EDGE,"E10.9.8.8"),sQuery(id+"F0.wireOp",EDGE,"E10.0.8.9"),sQuery(id+"F0.wireOp",EDGE,"E10.3.8.9"),sQuery(id+"F0.wireOp",EDGE,"E10.6.8.9"),sQuery(id+"F0.wireOp",EDGE,"E10.9.8.9"),sQuery(id+"F0.wireOp",EDGE,"E10.0.8.10"),sQuery(id+"F0.wireOp",EDGE,"E10.3.8.10"),sQuery(id+"F0.wireOp",EDGE,"E10.6.8.10"),sQuery(id+"F0.wireOp",EDGE,"E10.9.8.10"),sQuery(id+"F0.wireOp",EDGE,"E10.0.8.11"),sQuery(id+"F0.wireOp",EDGE,"E10.3.8.11"),sQuery(id+"F0.wireOp",EDGE,"E10.6.8.11"),sQuery(id+"F0.wireOp",EDGE,"E10.9.8.11"),sQuery(id+"F0.wireOp",EDGE,"E10.0.8.12"),sQuery(id+"F0.wireOp",EDGE,"E10.3.8.12"),sQuery(id+"F0.wireOp",EDGE,"E10.6.8.12"),sQuery(id+"F0.wireOp",EDGE,"E10.9.8.12"),sQuery(id+"F0.wireOp",EDGE,"E10.0.8.13"),sQuery(id+"F0.wireOp",EDGE,"E10.3.8.13"),sQuery(id+"F0.wireOp",EDGE,"E10.6.8.13"),sQuery(id+"F0.wireOp",EDGE,"E10.9.8.13"),sQuery(id+"F0.wireOp",EDGE,"E10.0.8.14"),sQuery(id+"F0.wireOp",EDGE,"E10.3.8.14"),sQuery(id+"F0.wireOp",EDGE,"E10.6.8.14"),sQuery(id+"F0.wireOp",EDGE,"E10.9.8.14"),sQuery(id+"F0.wireOp",EDGE,"E10.0.9.8"),sQuery(id+"F0.wireOp",EDGE,"E10.3.9.8"),sQuery(id+"F0.wireOp",EDGE,"E10.6.9.8"),sQuery(id+"F0.wireOp",EDGE,"E10.9.9.8"),sQuery(id+"F0.wireOp",EDGE,"E10.0.9.9"),sQuery(id+"F0.wireOp",EDGE,"E10.3.9.9"),sQuery(id+"F0.wireOp",EDGE,"E10.6.9.9"),sQuery(id+"F0.wireOp",EDGE,"E10.9.9.9"),sQuery(id+"F0.wireOp",EDGE,"E10.0.9.10"),sQuery(id+"F0.wireOp",EDGE,"E10.3.9.10"),sQuery(id+"F0.wireOp",EDGE,"E10.6.9.10"),sQuery(id+"F0.wireOp",EDGE,"E10.9.9.10"),sQuery(id+"F0.wireOp",EDGE,"E10.0.9.11"),sQuery(id+"F0.wireOp",EDGE,"E10.3.9.11"),sQuery(id+"F0.wireOp",EDGE,"E10.6.9.11"),sQuery(id+"F0.wireOp",EDGE,"E10.9.9.11"),sQuery(id+"F0.wireOp",EDGE,"E10.0.9.12"),sQuery(id+"F0.wireOp",EDGE,"E10.3.9.12"),sQuery(id+"F0.wireOp",EDGE,"E10.6.9.12"),sQuery(id+"F0.wireOp",EDGE,"E10.9.9.12"),sQuery(id+"F0.wireOp",EDGE,"E10.0.9.13"),sQuery(id+"F0.wireOp",EDGE,"E10.3.9.13"),sQuery(id+"F0.wireOp",EDGE,"E10.6.9.13"),sQuery(id+"F0.wireOp",EDGE,"E10.9.9.13"),sQuery(id+"F0.wireOp",EDGE,"E10.0.9.14"),sQuery(id+"F0.wireOp",EDGE,"E10.3.9.14"),sQuery(id+"F0.wireOp",EDGE,"E10.6.9.14"),sQuery(id+"F0.wireOp",EDGE,"E10.9.9.14"),sQuery(id+"F0.wireOp",EDGE,"E10.0.10.8"),sQuery(id+"F0.wireOp",EDGE,"E10.3.10.8"),sQuery(id+"F0.wireOp",EDGE,"E10.6.10.8"),sQuery(id+"F0.wireOp",EDGE,"E10.9.10.8"),sQuery(id+"F0.wireOp",EDGE,"E10.0.10.9"),sQuery(id+"F0.wireOp",EDGE,"E10.3.10.9"),sQuery(id+"F0.wireOp",EDGE,"E10.6.10.9"),sQuery(id+"F0.wireOp",EDGE,"E10.9.10.9"),sQuery(id+"F0.wireOp",EDGE,"E10.0.10.10"),sQuery(id+"F0.wireOp",EDGE,"E10.3.10.10"),sQuery(id+"F0.wireOp",EDGE,"E10.6.10.10"),sQuery(id+"F0.wireOp",EDGE,"E10.9.10.10"),sQuery(id+"F0.wireOp",EDGE,"E10.0.10.11"),sQuery(id+"F0.wireOp",EDGE,"E10.3.10.11"),sQuery(id+"F0.wireOp",EDGE,"E10.6.10.11"),sQuery(id+"F0.wireOp",EDGE,"E10.9.10.11"),sQuery(id+"F0.wireOp",EDGE,"E10.0.10.12"),sQuery(id+"F0.wireOp",EDGE,"E10.3.10.12"),sQuery(id+"F0.wireOp",EDGE,"E10.6.10.12"),sQuery(id+"F0.wireOp",EDGE,"E10.9.10.12"),sQuery(id+"F0.wireOp",EDGE,"E10.0.10.13"),sQuery(id+"F0.wireOp",EDGE,"E10.3.10.13"),sQuery(id+"F0.wireOp",EDGE,"E10.6.10.13"),sQuery(id+"F0.wireOp",EDGE,"E10.9.10.13"),sQuery(id+"F0.wireOp",EDGE,"E10.0.10.14"),sQuery(id+"F0.wireOp",EDGE,"E10.3.10.14"),sQuery(id+"F0.wireOp",EDGE,"E10.6.10.14"),sQuery(id+"F0.wireOp",EDGE,"E10.9.10.14"),sQuery(id+"F0.wireOp",EDGE,"E10.0.11.8"),sQuery(id+"F0.wireOp",EDGE,"E10.3.11.8"),sQuery(id+"F0.wireOp",EDGE,"E10.6.11.8"),sQuery(id+"F0.wireOp",EDGE,"E10.9.11.8"),sQuery(id+"F0.wireOp",EDGE,"E10.0.11.9"),sQuery(id+"F0.wireOp",EDGE,"E10.3.11.9"),sQuery(id+"F0.wireOp",EDGE,"E10.6.11.9"),sQuery(id+"F0.wireOp",EDGE,"E10.9.11.9"),sQuery(id+"F0.wireOp",EDGE,"E10.0.11.10"),sQuery(id+"F0.wireOp",EDGE,"E10.3.11.10"),sQuery(id+"F0.wireOp",EDGE,"E10.6.11.10"),sQuery(id+"F0.wireOp",EDGE,"E10.9.11.10"),sQuery(id+"F0.wireOp",EDGE,"E10.0.11.11"),sQuery(id+"F0.wireOp",EDGE,"E10.3.11.11"),sQuery(id+"F0.wireOp",EDGE,"E10.6.11.11"),sQuery(id+"F0.wireOp",EDGE,"E10.9.11.11"),sQuery(id+"F0.wireOp",EDGE,"E10.0.11.12"),sQuery(id+"F0.wireOp",EDGE,"E10.3.11.12"),sQuery(id+"F0.wireOp",EDGE,"E10.6.11.12"),sQuery(id+"F0.wireOp",EDGE,"E10.9.11.12"),sQuery(id+"F0.wireOp",EDGE,"E10.0.11.13"),sQuery(id+"F0.wireOp",EDGE,"E10.3.11.13"),sQuery(id+"F0.wireOp",EDGE,"E10.6.11.13"),sQuery(id+"F0.wireOp",EDGE,"E10.9.11.13"),sQuery(id+"F0.wireOp",EDGE,"E10.0.11.14"),sQuery(id+"F0.wireOp",EDGE,"E10.3.11.14"),sQuery(id+"F0.wireOp",EDGE,"E10.6.11.14"),sQuery(id+"F0.wireOp",EDGE,"E10.9.11.14"),sQuery(id+"F0.wireOp",EDGE,"E10.0.12.8"),sQuery(id+"F0.wireOp",EDGE,"E10.3.12.8"),sQuery(id+"F0.wireOp",EDGE,"E10.6.12.8"),sQuery(id+"F0.wireOp",EDGE,"E10.9.12.8"),sQuery(id+"F0.wireOp",EDGE,"E10.0.12.9"),sQuery(id+"F0.wireOp",EDGE,"E10.3.12.9"),sQuery(id+"F0.wireOp",EDGE,"E10.6.12.9"),sQuery(id+"F0.wireOp",EDGE,"E10.9.12.9"),sQuery(id+"F0.wireOp",EDGE,"E10.0.12.10"),sQuery(id+"F0.wireOp",EDGE,"E10.3.12.10"),sQuery(id+"F0.wireOp",EDGE,"E10.6.12.10"),sQuery(id+"F0.wireOp",EDGE,"E10.9.12.10"),sQuery(id+"F0.wireOp",EDGE,"E10.0.12.11"),sQuery(id+"F0.wireOp",EDGE,"E10.3.12.11"),sQuery(id+"F0.wireOp",EDGE,"E10.6.12.11"),sQuery(id+"F0.wireOp",EDGE,"E10.9.12.11"),sQuery(id+"F0.wireOp",EDGE,"E10.0.12.12"),sQuery(id+"F0.wireOp",EDGE,"E10.3.12.12"),sQuery(id+"F0.wireOp",EDGE,"E10.6.12.12"),sQuery(id+"F0.wireOp",EDGE,"E10.9.12.12"),sQuery(id+"F0.wireOp",EDGE,"E10.0.12.13"),sQuery(id+"F0.wireOp",EDGE,"E10.3.12.13"),sQuery(id+"F0.wireOp",EDGE,"E10.6.12.13"),sQuery(id+"F0.wireOp",EDGE,"E10.9.12.13"),sQuery(id+"F0.wireOp",EDGE,"E10.0.12.14"),sQuery(id+"F0.wireOp",EDGE,"E10.3.12.14"),sQuery(id+"F0.wireOp",EDGE,"E10.6.12.14"),sQuery(id+"F0.wireOp",EDGE,"E10.9.12.14"),sQuery(id+"F0.wireOp",EDGE,"E10.0.13.8"),sQuery(id+"F0.wireOp",EDGE,"E10.3.13.8"),sQuery(id+"F0.wireOp",EDGE,"E10.6.13.8"),sQuery(id+"F0.wireOp",EDGE,"E10.9.13.8"),sQuery(id+"F0.wireOp",EDGE,"E10.0.13.9"),sQuery(id+"F0.wireOp",EDGE,"E10.3.13.9"),sQuery(id+"F0.wireOp",EDGE,"E10.6.13.9"),sQuery(id+"F0.wireOp",EDGE,"E10.9.13.9"),sQuery(id+"F0.wireOp",EDGE,"E10.0.13.10"),sQuery(id+"F0.wireOp",EDGE,"E10.3.13.10"),sQuery(id+"F0.wireOp",EDGE,"E10.6.13.10"),sQuery(id+"F0.wireOp",EDGE,"E10.9.13.10"),sQuery(id+"F0.wireOp",EDGE,"E10.0.13.11"),sQuery(id+"F0.wireOp",EDGE,"E10.3.13.11"),sQuery(id+"F0.wireOp",EDGE,"E10.6.13.11"),sQuery(id+"F0.wireOp",EDGE,"E10.9.13.11"),sQuery(id+"F0.wireOp",EDGE,"E10.0.13.12"),sQuery(id+"F0.wireOp",EDGE,"E10.3.13.12"),sQuery(id+"F0.wireOp",EDGE,"E10.6.13.12"),sQuery(id+"F0.wireOp",EDGE,"E10.9.13.12"),sQuery(id+"F0.wireOp",EDGE,"E10.0.13.13"),sQuery(id+"F0.wireOp",EDGE,"E10.3.13.13"),sQuery(id+"F0.wireOp",EDGE,"E10.6.13.13"),sQuery(id+"F0.wireOp",EDGE,"E10.9.13.13"),sQuery(id+"F0.wireOp",EDGE,"E10.0.13.14"),sQuery(id+"F0.wireOp",EDGE,"E10.3.13.14"),sQuery(id+"F0.wireOp",EDGE,"E10.6.13.14"),sQuery(id+"F0.wireOp",EDGE,"E10.9.13.14"),sQuery(id+"F0.wireOp",EDGE,"E10.0.14.8"),sQuery(id+"F0.wireOp",EDGE,"E10.3.14.8"),sQuery(id+"F0.wireOp",EDGE,"E10.6.14.8"),sQuery(id+"F0.wireOp",EDGE,"E10.9.14.8"),sQuery(id+"F0.wireOp",EDGE,"E10.0.14.9"),sQuery(id+"F0.wireOp",EDGE,"E10.3.14.9"),sQuery(id+"F0.wireOp",EDGE,"E10.6.14.9"),sQuery(id+"F0.wireOp",EDGE,"E10.9.14.9"),sQuery(id+"F0.wireOp",EDGE,"E10.0.14.10"),sQuery(id+"F0.wireOp",EDGE,"E10.3.14.10"),sQuery(id+"F0.wireOp",EDGE,"E10.6.14.10"),sQuery(id+"F0.wireOp",EDGE,"E10.9.14.10"),sQuery(id+"F0.wireOp",EDGE,"E10.0.14.11"),sQuery(id+"F0.wireOp",EDGE,"E10.3.14.11"),sQuery(id+"F0.wireOp",EDGE,"E10.6.14.11"),sQuery(id+"F0.wireOp",EDGE,"E10.9.14.11"),sQuery(id+"F0.wireOp",EDGE,"E10.0.14.12"),sQuery(id+"F0.wireOp",EDGE,"E10.3.14.12"),sQuery(id+"F0.wireOp",EDGE,"E10.6.14.12"),sQuery(id+"F0.wireOp",EDGE,"E10.9.14.12"),sQuery(id+"F0.wireOp",EDGE,"E10.0.14.13"),sQuery(id+"F0.wireOp",EDGE,"E10.3.14.13"),sQuery(id+"F0.wireOp",EDGE,"E10.6.14.13"),sQuery(id+"F0.wireOp",EDGE,"E10.9.14.13"),sQuery(id+"F0.wireOp",EDGE,"E10.0.14.14"),sQuery(id+"F0.wireOp",EDGE,"E10.3.14.14"),sQuery(id+"F0.wireOp",EDGE,"E10.6.14.14"),sQuery(id+"F0.wireOp",EDGE,"E10.9.14.14")])],"isStart":false});
            var sketch = newSketch(context, id + "F3", { "sketchPlane" : qUnion([Q0])});
            skLineSegment(sketch, "E11", {"start": v(28, -34) * mm, "end": v(28, -33) * mm});
            skLineSegment(sketch, "E12", {"start": v(32, -29) * mm, "end": v(33, -29) * mm});
            skLineSegment(sketch, "E13", {"start": v(37, -33) * mm, "end": v(37, -34) * mm});
            skLineSegment(sketch, "E14", {"start": v(33, -38) * mm, "end": v(32, -38) * mm});
            skLineSegment(sketch, "E15", {"start": v(32, 36) * mm, "end": v(33, 36) * mm});
            skLineSegment(sketch, "E16", {"start": v(37, 32) * mm, "end": v(37, 31) * mm});
            skLineSegment(sketch, "E17", {"start": v(33, 27) * mm, "end": v(32, 27) * mm});
            skLineSegment(sketch, "E18", {"start": v(28, 31) * mm, "end": v(28, 32) * mm});
            skLineSegment(sketch, "E19", {"start": v(-28, 32) * mm, "end": v(-28, 31) * mm});
            skLineSegment(sketch, "E20", {"start": v(-32, 27) * mm, "end": v(-33, 27) * mm});
            skLineSegment(sketch, "E21", {"start": v(-37, 31) * mm, "end": v(-37, 32) * mm});
            skLineSegment(sketch, "E22", {"start": v(-33, 36) * mm, "end": v(-32, 36) * mm});
            skLineSegment(sketch, "E23", {"start": v(-33, -29) * mm, "end": v(-32, -29) * mm});
            skLineSegment(sketch, "E24", {"start": v(-28, -33) * mm, "end": v(-28, -34) * mm});
            skLineSegment(sketch, "E25", {"start": v(-32, -38) * mm, "end": v(-33, -38) * mm});
            skLineSegment(sketch, "E26", {"start": v(-37, -34) * mm, "end": v(-37, -33) * mm});
            skLineSegment(sketch, "E27", {"start": v(-3, 2) * mm, "end": v(-3, -4) * mm});
            skLineSegment(sketch, "E28", {"start": v(-3, -4) * mm, "end": v(3, -4) * mm});
            skLineSegment(sketch, "E29", {"start": v(3, -4) * mm, "end": v(3, 2) * mm});
            skLineSegment(sketch, "E30", {"start": v(3, 2) * mm, "end": v(-3, 2) * mm});
            skSolve(sketch);
        }
        {
            var Q0;
            Q0=makeQuery(id+"F3.imprint","IMPRINT",FACE,{"disambiguationData":[TD([[makeQuery(id+"F3.imprint","IMPRINT",EDGE,{"derivedFrom":sQuery(id+"F3.wireOp",EDGE,"E11")}),-1.0]])]});
            var Q1;
            Q1=makeQuery(id+"F3.imprint","IMPRINT",FACE,{"disambiguationData":[TD([[makeQuery(id+"F3.imprint","IMPRINT",EDGE,{"derivedFrom":sQuery(id+"F3.wireOp",EDGE,"E19")}),-1.0]])]});
            var Q2;
            Q2=makeQuery(id+"F3.imprint","IMPRINT",FACE,{"disambiguationData":[TD([[makeQuery(id+"F3.imprint","IMPRINT",EDGE,{"derivedFrom":sQuery(id+"F3.wireOp",EDGE,"E15")}),-1.0]])]});
            var Q3;
            Q3=makeQuery(id+"F3.imprint","IMPRINT",FACE,{"disambiguationData":[TD([[makeQuery(id+"F3.imprint","IMPRINT",EDGE,{"derivedFrom":sQuery(id+"F3.wireOp",EDGE,"E23")}),-1.0]])]});
            var Q4;
            Q4=makeQuery(id+"F3.imprint","IMPRINT",FACE,{"disambiguationData":[TD([[makeQuery(id+"F3.imprint","IMPRINT",EDGE,{"derivedFrom":makeQuery(id+"F1.opExtrude","CAP_EDGE",EDGE,{"disambiguationData":[OSD([sQuery(id+"F0.wireOp",EDGE,"E2.7.7.0")])],"isStart":false})}),1.0]])]});
            extrude(context, id + "F4", {"entities" : qUnion([Q0, Q1, Q2, Q3, Q4]), "operationType" : NewBodyOperationType.ADD, "depth" : 6 * mm, "offsetDistance" : 25 * mm});
        }
    });
